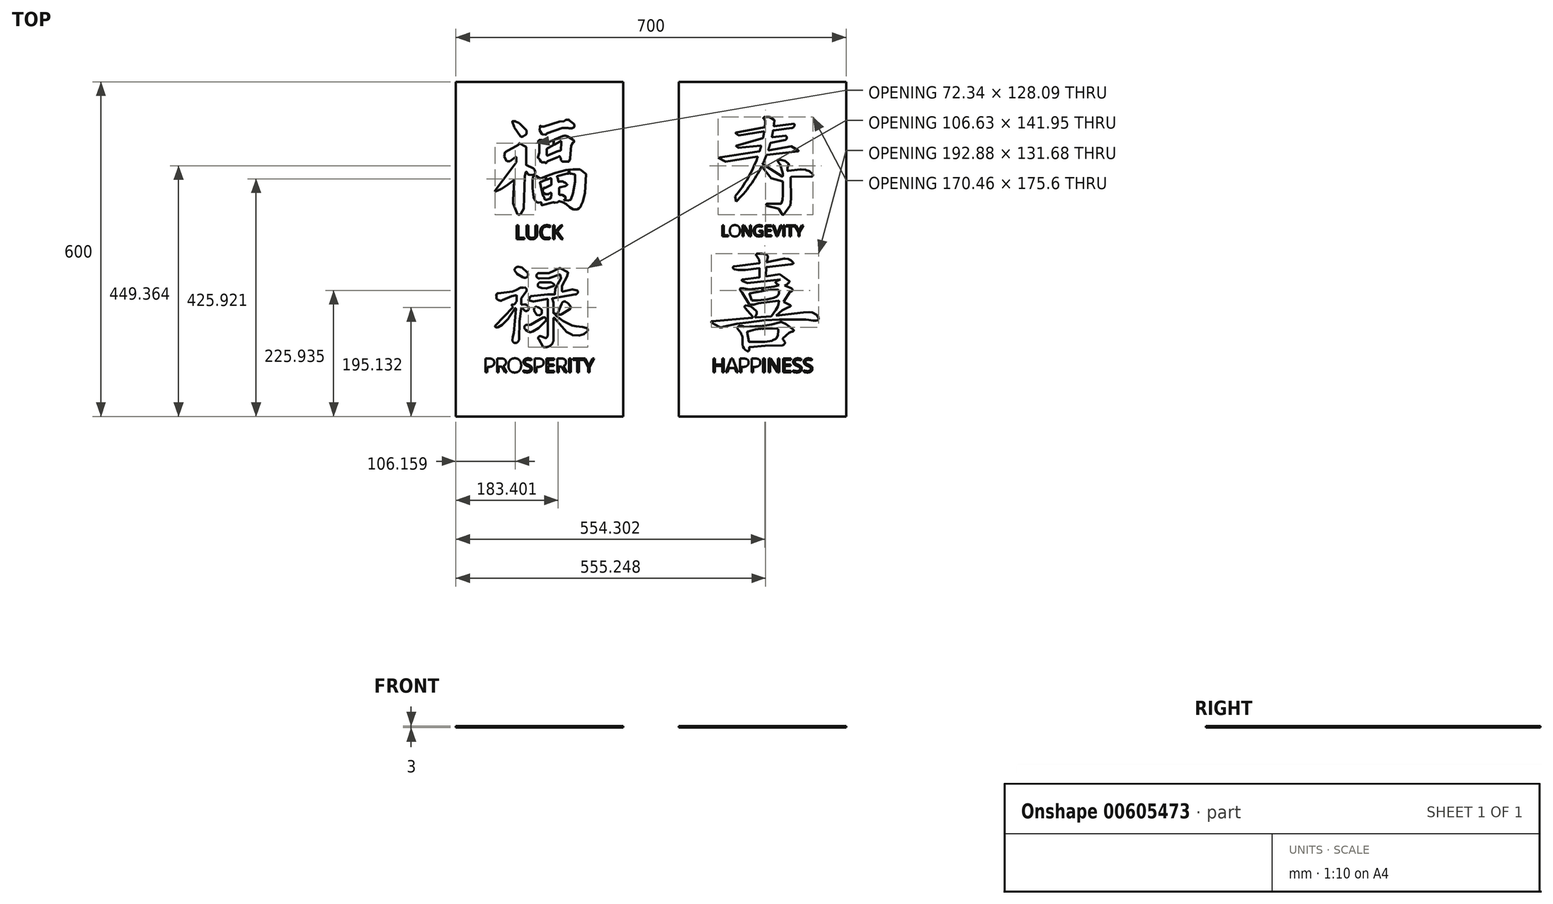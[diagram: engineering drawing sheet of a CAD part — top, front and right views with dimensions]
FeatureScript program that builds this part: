
annotation { "Feature Type Name" : "Feature", "Feature Type Description" : "" }
export const myFeature = defineFeature(function(context is Context, id is Id, definition is map)
    precondition{}
    {
        {
            var Q0;
            Q0=qCreatedBy(makeId("Top.planeOp"),FACE);
            var sketch = newSketch(context, id + "F0", { "sketchPlane" : qUnion([Q0])});
            skLineSegment(sketch, "E0.bottom", {"start": v(-350, 0) * mm, "end": v(-50, 0) * mm});
            skLineSegment(sketch, "E0.top", {"start": v(-350, -600) * mm, "end": v(-50, -600) * mm});
            skLineSegment(sketch, "E0.left", {"start": v(-350, 0) * mm, "end": v(-350, -600) * mm});
            skLineSegment(sketch, "E0.right", {"start": v(-50, 0) * mm, "end": v(-50, -600) * mm});
            skLineSegment(sketch, "E1.bottom", {"start": v(50, 0) * mm, "end": v(350, 0) * mm});
            skLineSegment(sketch, "E1.top", {"start": v(50, -600) * mm, "end": v(350, -600) * mm});
            skLineSegment(sketch, "E1.left", {"start": v(50, 0) * mm, "end": v(50, -600) * mm});
            skLineSegment(sketch, "E1.right", {"start": v(350, 0) * mm, "end": v(350, -600) * mm});
            skPoint(sketch, "E2", {"position": v(200, -322.19) * mm});
            skPoint(sketch, "E3", {"position": v(200, 889.4) * mm});
            skPoint(sketch, "E4", {"position": v(-200, -50.96) * mm});
            skPoint(sketch, "E5", {"position": v(-200, -322.19) * mm});
            skPoint(sketch, "E6", {"position": v(-200, 0) * mm});
            skPoint(sketch, "E7", {"position": v(200, 0) * mm});
            skArc(sketch, "E8", {"start": v(150.97, -205.38) * mm, "mid": v(173.95, -172.12) * mm, "end": v(191.01, -135.48) * mm});
            skLineSegment(sketch, "E9", {"start": v(203.27, -81.17) * mm, "end": v(152.4, -90.81) * mm});
            skLineSegment(sketch, "E10", {"start": v(152.1, -92.04) * mm, "end": v(157.18, -95.91) * mm});
            skLineSegment(sketch, "E11", {"start": v(157.7, -96.04) * mm, "end": v(201.62, -88.88) * mm});
            skLineSegment(sketch, "E12", {"start": v(200.2, -101.22) * mm, "end": v(153.27, -114.59) * mm});
            skLineSegment(sketch, "E13", {"start": v(153.04, -115.8) * mm, "end": v(155.79, -117.9) * mm});
            skLineSegment(sketch, "E14", {"start": v(156.27, -118.03) * mm, "end": v(196.3, -114.2) * mm});
            skLineSegment(sketch, "E15", {"start": v(194.19, -124.37) * mm, "end": v(120.02, -135.85) * mm});
            skLineSegment(sketch, "E16", {"start": v(120.02, -135.85) * mm, "end": v(133.53, -142.76) * mm});
            skLineSegment(sketch, "E17", {"start": v(133.94, -142.83) * mm, "end": v(189.92, -134.14) * mm});
            skArc(sketch, "E18", {"start": v(152.3, -214.99) * mm, "mid": v(178.07, -185.08) * mm, "end": v(198.4, -151.23) * mm});
            skPoint(sketch, "E19.visualSharp", {"position": v(150.97, -216.28) * mm});
            skPoint(sketch, "E20.visualSharp", {"position": v(133.72, -142.87) * mm});
            skArc(sketch, "E20.filletArc", {"start": v(133.53, -142.76) * mm, "mid": v(133.73, -142.83) * mm, "end": v(133.94, -142.83) * mm});
            skPoint(sketch, "E21.visualSharp", {"position": v(150.88, -91.1) * mm});
            skArc(sketch, "E21.filletArc", {"start": v(152.4, -90.81) * mm, "mid": v(151.85, -91.33) * mm, "end": v(152.1, -92.04) * mm});
            skPoint(sketch, "E22.visualSharp", {"position": v(157.41, -96.1) * mm});
            skArc(sketch, "E22.filletArc", {"start": v(157.18, -95.91) * mm, "mid": v(157.43, -96.03) * mm, "end": v(157.7, -96.04) * mm});
            skPoint(sketch, "E23.visualSharp", {"position": v(151.95, -114.96) * mm});
            skArc(sketch, "E23.filletArc", {"start": v(153.27, -114.59) * mm, "mid": v(152.78, -115.12) * mm, "end": v(153.04, -115.8) * mm});
            skPoint(sketch, "E24.visualSharp", {"position": v(156, -118.06) * mm});
            skArc(sketch, "E24.filletArc", {"start": v(155.79, -117.9) * mm, "mid": v(156.02, -118) * mm, "end": v(156.27, -118.03) * mm});
            skLineSegment(sketch, "E25", {"start": v(221.32, -79.5) * mm, "end": v(256.8, -75.2) * mm});
            skLineSegment(sketch, "E26", {"start": v(219.7, -86.87) * mm, "end": v(252.22, -82.93) * mm});
            skLineSegment(sketch, "E27", {"start": v(217.95, -99.22) * mm, "end": v(240.6, -96.47) * mm});
            skLineSegment(sketch, "E28", {"start": v(214.7, -109.29) * mm, "end": v(240.46, -104.07) * mm});
            skPoint(sketch, "E29.visualSharp", {"position": v(243.08, -103.54) * mm});
            skLineSegment(sketch, "E30", {"start": v(211.69, -122.58) * mm, "end": v(251.31, -115.55) * mm});
            skLineSegment(sketch, "E31", {"start": v(252, -115.67) * mm, "end": v(264.03, -122.7) * mm});
            skLineSegment(sketch, "E32", {"start": v(263.63, -124.55) * mm, "end": v(207.84, -130.7) * mm});
            skPoint(sketch, "E33.visualSharp", {"position": v(251.67, -115.49) * mm});
            skArc(sketch, "E33.filletArc", {"start": v(252, -115.67) * mm, "mid": v(251.66, -115.55) * mm, "end": v(251.31, -115.55) * mm});
            skPoint(sketch, "E34.visualSharp", {"position": v(266.64, -124.22) * mm});
            skArc(sketch, "E34.filletArc", {"start": v(263.63, -124.55) * mm, "mid": v(264.5, -123.76) * mm, "end": v(264.03, -122.7) * mm});
            skLineSegment(sketch, "E35", {"start": v(220.56, -75.45) * mm, "end": v(221.27, -69.14) * mm});
            skLineSegment(sketch, "E36", {"start": v(220.8, -68.17) * mm, "end": v(212.05, -62.97) * mm});
            skLineSegment(sketch, "E37", {"start": v(211.54, -62.83) * mm, "end": v(204.36, -62.83) * mm});
            skLineSegment(sketch, "E38", {"start": v(204.65, -74.72) * mm, "end": v(204.65, -69.48) * mm});
            skLineSegment(sketch, "E39", {"start": v(204.34, -68.75) * mm, "end": v(201.84, -66.36) * mm});
            skArc(sketch, "E40", {"start": v(204.36, -62.83) * mm, "mid": v(202.37, -63.65) * mm, "end": v(201.53, -65.62) * mm});
            skPoint(sketch, "E41.visualSharp", {"position": v(201.56, -66.1) * mm});
            skArc(sketch, "E41.filletArc", {"start": v(201.53, -65.62) * mm, "mid": v(201.6, -66.02) * mm, "end": v(201.84, -66.36) * mm});
            skPoint(sketch, "E42.visualSharp", {"position": v(211.82, -62.83) * mm});
            skArc(sketch, "E42.filletArc", {"start": v(212.05, -62.97) * mm, "mid": v(211.8, -62.87) * mm, "end": v(211.54, -62.83) * mm});
            skPoint(sketch, "E43.visualSharp", {"position": v(221.35, -68.5) * mm});
            skArc(sketch, "E43.filletArc", {"start": v(221.27, -69.14) * mm, "mid": v(221.18, -68.58) * mm, "end": v(220.8, -68.17) * mm});
            skPoint(sketch, "E44.visualSharp", {"position": v(204.65, -69.05) * mm});
            skArc(sketch, "E44.filletArc", {"start": v(204.65, -69.48) * mm, "mid": v(204.57, -69.08) * mm, "end": v(204.34, -68.75) * mm});
            skArc(sketch, "E45.trimOffspring", {"start": v(220.2, -78.38) * mm, "mid": v(220.38, -76.92) * mm, "end": v(220.56, -75.45) * mm});
            skArc(sketch, "E46.trimOffspring", {"start": v(204.08, -80.3) * mm, "mid": v(204.38, -77.5) * mm, "end": v(204.65, -74.72) * mm});
            skArc(sketch, "E47.trimOffspring", {"start": v(216.85, -98.01) * mm, "mid": v(217.9, -92.87) * mm, "end": v(218.83, -87.7) * mm});
            skArc(sketch, "E48.trimOffspring", {"start": v(200.9, -100.46) * mm, "mid": v(201.9, -95.25) * mm, "end": v(202.77, -90.02) * mm});
            skArc(sketch, "E49.trimOffspring", {"start": v(210.56, -121.28) * mm, "mid": v(212.32, -115.66) * mm, "end": v(213.94, -110) * mm});
            skArc(sketch, "E50.trimOffspring", {"start": v(195, -123.67) * mm, "mid": v(196.22, -119.58) * mm, "end": v(197.37, -115.46) * mm});
            skPoint(sketch, "E51.visualSharp", {"position": v(204, -81.03) * mm});
            skArc(sketch, "E51.filletArc", {"start": v(203.27, -81.17) * mm, "mid": v(203.82, -80.87) * mm, "end": v(204.08, -80.3) * mm});
            skPoint(sketch, "E52.visualSharp", {"position": v(220.04, -79.65) * mm});
            skArc(sketch, "E52.filletArc", {"start": v(220.2, -78.38) * mm, "mid": v(220.49, -79.21) * mm, "end": v(221.32, -79.5) * mm});
            skPoint(sketch, "E53.visualSharp", {"position": v(218.95, -86.96) * mm});
            skArc(sketch, "E53.filletArc", {"start": v(219.7, -86.87) * mm, "mid": v(219.12, -87.14) * mm, "end": v(218.83, -87.7) * mm});
            skArc(sketch, "E54.filletArc", {"start": v(202.77, -90.02) * mm, "mid": v(202.48, -89.15) * mm, "end": v(201.62, -88.88) * mm});
            skPoint(sketch, "E55.visualSharp", {"position": v(214.1, -109.4) * mm});
            skArc(sketch, "E55.filletArc", {"start": v(214.7, -109.29) * mm, "mid": v(214.22, -109.54) * mm, "end": v(213.94, -110) * mm});
            skPoint(sketch, "E56.visualSharp", {"position": v(216.55, -99.39) * mm});
            skArc(sketch, "E56.filletArc", {"start": v(216.85, -98.01) * mm, "mid": v(217.1, -98.9) * mm, "end": v(217.95, -99.22) * mm});
            skPoint(sketch, "E57.visualSharp", {"position": v(200.78, -101.06) * mm});
            skArc(sketch, "E57.filletArc", {"start": v(200.2, -101.22) * mm, "mid": v(200.65, -100.94) * mm, "end": v(200.9, -100.46) * mm});
            skPoint(sketch, "E58.visualSharp", {"position": v(197.74, -114.07) * mm});
            skArc(sketch, "E58.filletArc", {"start": v(197.37, -115.46) * mm, "mid": v(197.16, -114.56) * mm, "end": v(196.3, -114.2) * mm});
            skPoint(sketch, "E59.visualSharp", {"position": v(210.04, -122.87) * mm});
            skArc(sketch, "E59.filletArc", {"start": v(210.56, -121.28) * mm, "mid": v(210.76, -122.25) * mm, "end": v(211.69, -122.58) * mm});
            skPoint(sketch, "E60.visualSharp", {"position": v(194.8, -124.27) * mm});
            skArc(sketch, "E60.filletArc", {"start": v(194.19, -124.37) * mm, "mid": v(194.69, -124.14) * mm, "end": v(195, -123.67) * mm});
            skPoint(sketch, "E61.visualSharp", {"position": v(207.23, -130.77) * mm});
            skArc(sketch, "E61.filletArc", {"start": v(207.84, -130.7) * mm, "mid": v(207.34, -130.91) * mm, "end": v(207.01, -131.35) * mm});
            skPoint(sketch, "E62.visualSharp", {"position": v(191.59, -133.88) * mm});
            skArc(sketch, "E62.filletArc", {"start": v(191.01, -135.48) * mm, "mid": v(190.85, -134.5) * mm, "end": v(189.92, -134.14) * mm});
            skLineSegment(sketch, "E63", {"start": v(236.4, -202.56) * mm, "end": v(236.4, -178.81) * mm});
            skLineSegment(sketch, "E64", {"start": v(236.35, -164.48) * mm, "end": v(231.15, -147.17) * mm});
            skLineSegment(sketch, "E65", {"start": v(230.92, -146.78) * mm, "end": v(226.96, -142.52) * mm});
            skLineSegment(sketch, "E66", {"start": v(228.2, -139.57) * mm, "end": v(232.25, -139.57) * mm});
            skLineSegment(sketch, "E67", {"start": v(232.54, -139.61) * mm, "end": v(240, -141.85) * mm});
            skLineSegment(sketch, "E68", {"start": v(240.3, -142) * mm, "end": v(246.08, -146.34) * mm});
            skLineSegment(sketch, "E69", {"start": v(246.46, -146.92) * mm, "end": v(246.91, -148.97) * mm});
            skLineSegment(sketch, "E70", {"start": v(246.8, -149.7) * mm, "end": v(244.96, -152.72) * mm});
            skLineSegment(sketch, "E71", {"start": v(244.82, -153.24) * mm, "end": v(244.82, -158.86) * mm});
            skLineSegment(sketch, "E72", {"start": v(245.95, -159.86) * mm, "end": v(268.33, -156.78) * mm});
            skLineSegment(sketch, "E73", {"start": v(268.6, -156.78) * mm, "end": v(277.5, -157.95) * mm});
            skLineSegment(sketch, "E74", {"start": v(277.7, -158) * mm, "end": v(283.92, -160.22) * mm});
            skLineSegment(sketch, "E75", {"start": v(284.29, -160.44) * mm, "end": v(290.1, -166.12) * mm});
            skLineSegment(sketch, "E76", {"start": v(287.91, -169.95) * mm, "end": v(251.6, -170.63) * mm});
            skLineSegment(sketch, "E77", {"start": v(250.6, -171.65) * mm, "end": v(251.33, -209.98) * mm});
            skLineSegment(sketch, "E78", {"start": v(251.33, -209.98) * mm, "end": v(251.22, -210.71) * mm});
            skLineSegment(sketch, "E79", {"start": v(251.22, -210.71) * mm, "end": v(249.58, -222.08) * mm});
            skLineSegment(sketch, "E80", {"start": v(249.38, -222.55) * mm, "end": v(237.4, -238.05) * mm});
            skLineSegment(sketch, "E81", {"start": v(235.76, -237.98) * mm, "end": v(228.89, -227.27) * mm});
            skLineSegment(sketch, "E82", {"start": v(228.89, -227.27) * mm, "end": v(208, -222.39) * mm});
            skLineSegment(sketch, "E83", {"start": v(208.92, -218.5) * mm, "end": v(233.02, -218.32) * mm});
            skLineSegment(sketch, "E84", {"start": v(233.98, -217.57) * mm, "end": v(235.56, -211.62) * mm});
            skLineSegment(sketch, "E85", {"start": v(235.6, -211.45) * mm, "end": v(236.4, -202.65) * mm});
            skArc(sketch, "E86", {"start": v(208.92, -218.5) * mm, "mid": v(206.52, -220) * mm, "end": v(208, -222.39) * mm});
            skLineSegment(sketch, "E87", {"start": v(234.87, -169.4) * mm, "end": v(200.05, -147.79) * mm});
            skLineSegment(sketch, "E88", {"start": v(198.4, -151.23) * mm, "end": v(215.23, -173.01) * mm});
            skPoint(sketch, "E89.visualSharp", {"position": v(210.3, -166.64) * mm});
            skPoint(sketch, "E90.visualSharp", {"position": v(232.83, -176.15) * mm});
            skPoint(sketch, "E91.visualSharp", {"position": v(231.08, -146.95) * mm});
            skArc(sketch, "E91.filletArc", {"start": v(231.15, -147.17) * mm, "mid": v(231.06, -146.96) * mm, "end": v(230.92, -146.78) * mm});
            skPoint(sketch, "E92.visualSharp", {"position": v(236.4, -164.62) * mm});
            skArc(sketch, "E92.filletArc", {"start": v(236.4, -164.77) * mm, "mid": v(236.39, -164.62) * mm, "end": v(236.35, -164.48) * mm});
            skPoint(sketch, "E93.visualSharp", {"position": v(244.82, -152.96) * mm});
            skArc(sketch, "E93.filletArc", {"start": v(244.96, -152.72) * mm, "mid": v(244.85, -152.97) * mm, "end": v(244.82, -153.24) * mm});
            skPoint(sketch, "E94.visualSharp", {"position": v(247, -149.36) * mm});
            skArc(sketch, "E94.filletArc", {"start": v(246.8, -149.7) * mm, "mid": v(246.92, -149.35) * mm, "end": v(246.91, -148.97) * mm});
            skPoint(sketch, "E95.visualSharp", {"position": v(246.38, -146.56) * mm});
            skArc(sketch, "E95.filletArc", {"start": v(246.46, -146.92) * mm, "mid": v(246.32, -146.6) * mm, "end": v(246.08, -146.34) * mm});
            skPoint(sketch, "E96.visualSharp", {"position": v(240.17, -141.9) * mm});
            skArc(sketch, "E96.filletArc", {"start": v(240.3, -142) * mm, "mid": v(240.16, -141.92) * mm, "end": v(240, -141.85) * mm});
            skPoint(sketch, "E97.visualSharp", {"position": v(232.4, -139.57) * mm});
            skArc(sketch, "E97.filletArc", {"start": v(232.54, -139.61) * mm, "mid": v(232.4, -139.58) * mm, "end": v(232.25, -139.57) * mm});
            skArc(sketch, "E98", {"start": v(228.2, -139.57) * mm, "mid": v(226.63, -140.65) * mm, "end": v(226.96, -142.52) * mm});
            skLineSegment(sketch, "E99.trimOffspring", {"start": v(236.4, -168.56) * mm, "end": v(236.4, -164.77) * mm});
            skPoint(sketch, "E100.visualSharp", {"position": v(236.4, -170.36) * mm});
            skArc(sketch, "E100.filletArc", {"start": v(234.87, -169.4) * mm, "mid": v(235.88, -169.43) * mm, "end": v(236.4, -168.56) * mm});
            skPoint(sketch, "E101.visualSharp", {"position": v(244.82, -160.01) * mm});
            skArc(sketch, "E101.filletArc", {"start": v(244.82, -158.86) * mm, "mid": v(245.16, -159.62) * mm, "end": v(245.95, -159.86) * mm});
            skPoint(sketch, "E102.visualSharp", {"position": v(250.6, -170.65) * mm});
            skArc(sketch, "E102.filletArc", {"start": v(251.6, -170.63) * mm, "mid": v(250.89, -170.93) * mm, "end": v(250.6, -171.65) * mm});
            skPoint(sketch, "E103.visualSharp", {"position": v(236.4, -190.47) * mm});
            skPoint(sketch, "E104.visualSharp", {"position": v(268.46, -156.76) * mm});
            skArc(sketch, "E104.filletArc", {"start": v(268.6, -156.78) * mm, "mid": v(268.46, -156.77) * mm, "end": v(268.33, -156.78) * mm});
            skPoint(sketch, "E105.visualSharp", {"position": v(277.6, -157.96) * mm});
            skArc(sketch, "E105.filletArc", {"start": v(277.7, -158) * mm, "mid": v(277.6, -157.97) * mm, "end": v(277.5, -157.95) * mm});
            skPoint(sketch, "E106.visualSharp", {"position": v(284.13, -160.3) * mm});
            skArc(sketch, "E106.filletArc", {"start": v(284.29, -160.44) * mm, "mid": v(284.12, -160.31) * mm, "end": v(283.92, -160.22) * mm});
            skArc(sketch, "E107", {"start": v(287.91, -169.95) * mm, "mid": v(290, -168.85) * mm, "end": v(290.36, -166.53) * mm});
            skPoint(sketch, "E108.visualSharp", {"position": v(290.27, -166.27) * mm});
            skArc(sketch, "E108.filletArc", {"start": v(290.36, -166.53) * mm, "mid": v(290.26, -166.3) * mm, "end": v(290.1, -166.12) * mm});
            skPoint(sketch, "E109.visualSharp", {"position": v(235.58, -211.54) * mm});
            skArc(sketch, "E109.filletArc", {"start": v(235.56, -211.62) * mm, "mid": v(235.58, -211.54) * mm, "end": v(235.6, -211.45) * mm});
            skPoint(sketch, "E110.visualSharp", {"position": v(236.4, -202.6) * mm});
            skArc(sketch, "E110.filletArc", {"start": v(236.4, -202.65) * mm, "mid": v(236.4, -202.6) * mm, "end": v(236.4, -202.56) * mm});
            skPoint(sketch, "E111.visualSharp", {"position": v(233.78, -218.31) * mm});
            skArc(sketch, "E111.filletArc", {"start": v(233.02, -218.32) * mm, "mid": v(233.62, -218.1) * mm, "end": v(233.98, -217.57) * mm});
            skPoint(sketch, "E112.visualSharp", {"position": v(249.54, -222.34) * mm});
            skArc(sketch, "E112.filletArc", {"start": v(249.38, -222.55) * mm, "mid": v(249.51, -222.33) * mm, "end": v(249.58, -222.08) * mm});
            skPoint(sketch, "E113.visualSharp", {"position": v(250.6, -215.07) * mm});
            skLineSegment(sketch, "E113.filletArc", {"start": v(251.22, -210.71) * mm, "end": v(251.22, -210.71) * mm});
            skPoint(sketch, "E114.visualSharp", {"position": v(234.79, -236.46) * mm});
            skLineSegment(sketch, "E115", {"start": v(206.79, -324.76) * mm, "end": v(206.79, -322.64) * mm});
            skLineSegment(sketch, "E116", {"start": v(206.79, -324.76) * mm, "end": v(209.26, -315.5) * mm});
            skLineSegment(sketch, "E117", {"start": v(205.94, -309.66) * mm, "end": v(199.02, -308.22) * mm});
            skLineSegment(sketch, "E118", {"start": v(199.02, -308.22) * mm, "end": v(190.8, -308.22) * mm});
            skLineSegment(sketch, "E119", {"start": v(193.97, -318.77) * mm, "end": v(188.57, -311.62) * mm});
            skLineSegment(sketch, "E120", {"start": v(194.17, -319.3) * mm, "end": v(194.58, -324.5) * mm});
            skLineSegment(sketch, "E121", {"start": v(193.7, -325.58) * mm, "end": v(149.02, -330.78) * mm});
            skLineSegment(sketch, "E122", {"start": v(147.17, -334.1) * mm, "end": v(149.2, -336.14) * mm});
            skLineSegment(sketch, "E123", {"start": v(149.2, -336.14) * mm, "end": v(156.22, -337.61) * mm});
            skLineSegment(sketch, "E124", {"start": v(156.22, -337.61) * mm, "end": v(168.97, -337.61) * mm});
            skLineSegment(sketch, "E125", {"start": v(168.97, -337.61) * mm, "end": v(193.7, -334.35) * mm});
            skLineSegment(sketch, "E126", {"start": v(194.83, -335.34) * mm, "end": v(194.83, -349.81) * mm});
            skLineSegment(sketch, "E127", {"start": v(193.95, -350.8) * mm, "end": v(164.25, -354.23) * mm});
            skLineSegment(sketch, "E128", {"start": v(163.67, -357.23) * mm, "end": v(172.73, -360.64) * mm});
            skLineSegment(sketch, "E129", {"start": v(172.73, -360.64) * mm, "end": v(232.3, -354.46) * mm});
            skLineSegment(sketch, "E130", {"start": v(222.37, -357.99) * mm, "end": v(232.3, -354.46) * mm});
            skLineSegment(sketch, "E131", {"start": v(248.66, -357.47) * mm, "end": v(230.64, -345.03) * mm});
            skLineSegment(sketch, "E132", {"start": v(230.64, -345.03) * mm, "end": v(206.9, -348.46) * mm});
            skLineSegment(sketch, "E133", {"start": v(205.75, -347.43) * mm, "end": v(206.4, -332.96) * mm});
            skLineSegment(sketch, "E134", {"start": v(207.3, -332.01) * mm, "end": v(250.74, -327.37) * mm});
            skLineSegment(sketch, "E135", {"start": v(250.74, -327.37) * mm, "end": v(253.77, -326.67) * mm});
            skLineSegment(sketch, "E136", {"start": v(254.7, -323.72) * mm, "end": v(250.9, -320.07) * mm});
            skLineSegment(sketch, "E137", {"start": v(250.9, -320.07) * mm, "end": v(246.21, -317.94) * mm});
            skLineSegment(sketch, "E138", {"start": v(246.21, -317.94) * mm, "end": v(240.47, -317.15) * mm});
            skLineSegment(sketch, "E139", {"start": v(240.47, -317.15) * mm, "end": v(238.33, -317.15) * mm});
            skLineSegment(sketch, "E140", {"start": v(238.33, -317.15) * mm, "end": v(208, -323.62) * mm});
            skArc(sketch, "E141", {"start": v(222.37, -357.99) * mm, "mid": v(235.67, -365.74) * mm, "end": v(248.66, -357.47) * mm});
            skArc(sketch, "E142", {"start": v(253.77, -326.67) * mm, "mid": v(255.16, -325.49) * mm, "end": v(254.7, -323.72) * mm});
            skArc(sketch, "E143", {"start": v(209.26, -315.5) * mm, "mid": v(208.92, -311.83) * mm, "end": v(205.94, -309.66) * mm});
            skArc(sketch, "E144", {"start": v(190.8, -308.22) * mm, "mid": v(188.76, -309.32) * mm, "end": v(188.57, -311.62) * mm});
            skArc(sketch, "E145", {"start": v(149.02, -330.78) * mm, "mid": v(147.24, -331.97) * mm, "end": v(147.17, -334.1) * mm});
            skArc(sketch, "E146", {"start": v(164.25, -354.23) * mm, "mid": v(162.86, -355.52) * mm, "end": v(163.67, -357.23) * mm});
            skLineSegment(sketch, "E147", {"start": v(175.47, -372.3) * mm, "end": v(198.63, -369.76) * mm});
            skLineSegment(sketch, "E148", {"start": v(220.66, -367.34) * mm, "end": v(230.72, -363.81) * mm});
            skLineSegment(sketch, "E149", {"start": v(230.72, -363.81) * mm, "end": v(234.51, -363.81) * mm});
            skLineSegment(sketch, "E150", {"start": v(234.51, -363.81) * mm, "end": v(239.01, -364.72) * mm});
            skLineSegment(sketch, "E151", {"start": v(239.01, -364.72) * mm, "end": v(252.04, -370.48) * mm});
            skLineSegment(sketch, "E152", {"start": v(249.71, -375.74) * mm, "end": v(237.97, -394.34) * mm});
            skLineSegment(sketch, "E153", {"start": v(237.97, -394.34) * mm, "end": v(250.14, -401.01) * mm});
            skLineSegment(sketch, "E154", {"start": v(243.94, -405.05) * mm, "end": v(235.45, -409.87) * mm});
            skLineSegment(sketch, "E155", {"start": v(235.45, -409.87) * mm, "end": v(229.9, -413.94) * mm});
            skLineSegment(sketch, "E156", {"start": v(229.9, -413.94) * mm, "end": v(224.27, -419.57) * mm});
            skLineSegment(sketch, "E157", {"start": v(224.27, -419.57) * mm, "end": v(273.02, -413.63) * mm});
            skLineSegment(sketch, "E158", {"start": v(273.02, -413.63) * mm, "end": v(283.46, -412.76) * mm});
            skLineSegment(sketch, "E159", {"start": v(283.46, -412.76) * mm, "end": v(289.2, -413.54) * mm});
            skLineSegment(sketch, "E160", {"start": v(289.2, -413.54) * mm, "end": v(297.19, -417.92) * mm});
            skLineSegment(sketch, "E161", {"start": v(297.19, -417.92) * mm, "end": v(300.74, -422.77) * mm});
            skLineSegment(sketch, "E162", {"start": v(300.74, -422.77) * mm, "end": v(300.74, -425.73) * mm});
            skLineSegment(sketch, "E163", {"start": v(300.74, -425.73) * mm, "end": v(298.89, -427.59) * mm});
            skLineSegment(sketch, "E164", {"start": v(298.89, -427.59) * mm, "end": v(296.18, -428.14) * mm});
            skLineSegment(sketch, "E165", {"start": v(296.18, -428.14) * mm, "end": v(290.12, -428.14) * mm});
            skLineSegment(sketch, "E166", {"start": v(290.12, -428.14) * mm, "end": v(282.51, -426.82) * mm});
            skLineSegment(sketch, "E167", {"start": v(282.51, -426.82) * mm, "end": v(277.46, -425.97) * mm});
            skLineSegment(sketch, "E168", {"start": v(277.46, -425.97) * mm, "end": v(229.98, -425.97) * mm});
            skLineSegment(sketch, "E169", {"start": v(229.98, -425.97) * mm, "end": v(203.95, -427.55) * mm});
            skLineSegment(sketch, "E170", {"start": v(203.95, -427.55) * mm, "end": v(174.55, -431.17) * mm});
            skLineSegment(sketch, "E171", {"start": v(174.55, -431.17) * mm, "end": v(154.02, -434.06) * mm});
            skLineSegment(sketch, "E172", {"start": v(154.02, -434.06) * mm, "end": v(130.64, -439.15) * mm});
            skLineSegment(sketch, "E173", {"start": v(130.64, -439.15) * mm, "end": v(128.3, -439.86) * mm});
            skLineSegment(sketch, "E174", {"start": v(128.01, -439.9) * mm, "end": v(123.07, -439.9) * mm});
            skLineSegment(sketch, "E175", {"start": v(122.6, -439.78) * mm, "end": v(108.69, -432.16) * mm});
            skLineSegment(sketch, "E176", {"start": v(109.24, -429.14) * mm, "end": v(181.48, -423.06) * mm});
            skLineSegment(sketch, "E177", {"start": v(182.16, -421.42) * mm, "end": v(168.34, -404.98) * mm});
            skPoint(sketch, "E178", {"position": v(168.01, -402.4) * mm});
            skLineSegment(sketch, "E179", {"start": v(169.41, -401.14) * mm, "end": v(174.11, -401.53) * mm});
            skLineSegment(sketch, "E180", {"start": v(174.11, -401.53) * mm, "end": v(177.2, -402.04) * mm});
            skLineSegment(sketch, "E181", {"start": v(177.2, -402.04) * mm, "end": v(179.42, -403) * mm});
            skLineSegment(sketch, "E182", {"start": v(179.42, -403) * mm, "end": v(188.9, -411.09) * mm});
            skLineSegment(sketch, "E183", {"start": v(188.9, -411.09) * mm, "end": v(189.44, -412.41) * mm});
            skLineSegment(sketch, "E184", {"start": v(189.44, -412.41) * mm, "end": v(189.44, -416.06) * mm});
            skLineSegment(sketch, "E185", {"start": v(189.44, -416.06) * mm, "end": v(187.22, -421.36) * mm});
            skLineSegment(sketch, "E186", {"start": v(188.23, -422.74) * mm, "end": v(215.19, -420.24) * mm});
            skLineSegment(sketch, "E187", {"start": v(215.9, -419.84) * mm, "end": v(223.65, -409.38) * mm});
            skLineSegment(sketch, "E188", {"start": v(223.65, -409.38) * mm, "end": v(227.7, -402.55) * mm});
            skLineSegment(sketch, "E189", {"start": v(227.7, -402.55) * mm, "end": v(228.97, -397.84) * mm});
            skLineSegment(sketch, "E190", {"start": v(228.97, -397.84) * mm, "end": v(229.38, -393.54) * mm});
            skLineSegment(sketch, "E191", {"start": v(228.25, -392.45) * mm, "end": v(192.82, -397.1) * mm});
            skLineSegment(sketch, "E192", {"start": v(192.82, -397.1) * mm, "end": v(184.51, -399.27) * mm});
            skLineSegment(sketch, "E193", {"start": v(184.51, -399.27) * mm, "end": v(182.17, -399.5) * mm});
            skLineSegment(sketch, "E194", {"start": v(182.17, -399.5) * mm, "end": v(177.24, -399.5) * mm});
            skLineSegment(sketch, "E195", {"start": v(177.24, -399.5) * mm, "end": v(176.3, -399.08) * mm});
            skLineSegment(sketch, "E196", {"start": v(176.3, -399.08) * mm, "end": v(163.42, -378.13) * mm});
            skLineSegment(sketch, "E197", {"start": v(163.42, -378.13) * mm, "end": v(159.8, -373.41) * mm});
            skLineSegment(sketch, "E198", {"start": v(161.21, -370.13) * mm, "end": v(166.22, -370.13) * mm});
            skLineSegment(sketch, "E199", {"start": v(166.22, -370.13) * mm, "end": v(175.47, -372.3) * mm});
            skArc(sketch, "E200", {"start": v(161.21, -370.13) * mm, "mid": v(159.53, -371.35) * mm, "end": v(159.8, -373.41) * mm});
            skArc(sketch, "E201", {"start": v(249.71, -375.74) * mm, "mid": v(253.5, -374.27) * mm, "end": v(252.04, -370.48) * mm});
            skArc(sketch, "E202", {"start": v(168.01, -402.4) * mm, "mid": v(167.98, -403.71) * mm, "end": v(168.34, -404.98) * mm});
            skArc(sketch, "E203", {"start": v(168.76, -401.32) * mm, "mid": v(168.29, -401.79) * mm, "end": v(168.01, -402.4) * mm});
            skArc(sketch, "E204", {"start": v(109.24, -429.14) * mm, "mid": v(107.87, -430.45) * mm, "end": v(108.69, -432.16) * mm});
            skLineSegment(sketch, "E205", {"start": v(177.42, -379.2) * mm, "end": v(198.9, -375.5) * mm});
            skLineSegment(sketch, "E206", {"start": v(213.91, -372.92) * mm, "end": v(227.23, -372.92) * mm});
            skLineSegment(sketch, "E207", {"start": v(176.65, -380.51) * mm, "end": v(180.66, -392.03) * mm});
            skLineSegment(sketch, "E208", {"start": v(180.66, -392.03) * mm, "end": v(191.53, -392.03) * mm});
            skLineSegment(sketch, "E209", {"start": v(191.53, -392.03) * mm, "end": v(208.45, -389.83) * mm});
            skLineSegment(sketch, "E210", {"start": v(208.45, -389.83) * mm, "end": v(219.87, -387.3) * mm});
            skLineSegment(sketch, "E211", {"start": v(219.87, -387.3) * mm, "end": v(225.47, -385.22) * mm});
            skLineSegment(sketch, "E212", {"start": v(228.55, -381.04) * mm, "end": v(229.43, -378.63) * mm});
            skLineSegment(sketch, "E213", {"start": v(229.43, -378.63) * mm, "end": v(229.2, -374.78) * mm});
            skArc(sketch, "E214", {"start": v(225.47, -385.22) * mm, "mid": v(227.31, -383.35) * mm, "end": v(228.55, -381.04) * mm});
            skArc(sketch, "E215", {"start": v(229.2, -374.78) * mm, "mid": v(228.59, -373.46) * mm, "end": v(227.23, -372.92) * mm});
            skPoint(sketch, "E216.visualSharp", {"position": v(194.15, -319) * mm});
            skArc(sketch, "E216.filletArc", {"start": v(194.17, -319.3) * mm, "mid": v(194.11, -319.02) * mm, "end": v(193.97, -318.77) * mm});
            skPoint(sketch, "E217.visualSharp", {"position": v(206.79, -323.87) * mm});
            skArc(sketch, "E217.filletArc", {"start": v(206.79, -322.64) * mm, "mid": v(207.16, -323.42) * mm, "end": v(208, -323.62) * mm});
            skPoint(sketch, "E218.visualSharp", {"position": v(194.66, -325.47) * mm});
            skArc(sketch, "E218.filletArc", {"start": v(193.7, -325.58) * mm, "mid": v(194.36, -325.22) * mm, "end": v(194.58, -324.5) * mm});
            skPoint(sketch, "E219.visualSharp", {"position": v(206.44, -332.1) * mm});
            skArc(sketch, "E219.filletArc", {"start": v(207.3, -332.01) * mm, "mid": v(206.67, -332.32) * mm, "end": v(206.4, -332.96) * mm});
            skPoint(sketch, "E220.visualSharp", {"position": v(194.83, -334.2) * mm});
            skArc(sketch, "E220.filletArc", {"start": v(194.83, -335.34) * mm, "mid": v(194.49, -334.59) * mm, "end": v(193.7, -334.35) * mm});
            skPoint(sketch, "E221.visualSharp", {"position": v(205.7, -348.64) * mm});
            skArc(sketch, "E221.filletArc", {"start": v(205.75, -347.43) * mm, "mid": v(206.08, -348.22) * mm, "end": v(206.9, -348.46) * mm});
            skPoint(sketch, "E222.visualSharp", {"position": v(194.83, -350.7) * mm});
            skArc(sketch, "E222.filletArc", {"start": v(193.95, -350.8) * mm, "mid": v(194.58, -350.48) * mm, "end": v(194.83, -349.81) * mm});
            skPoint(sketch, "E223.visualSharp", {"position": v(176.26, -379.4) * mm});
            skArc(sketch, "E223.filletArc", {"start": v(177.42, -379.2) * mm, "mid": v(176.73, -379.67) * mm, "end": v(176.65, -380.51) * mm});
            skPoint(sketch, "E224.visualSharp", {"position": v(213.83, -372.92) * mm});
            skArc(sketch, "E224.filletArc", {"start": v(213.91, -372.92) * mm, "mid": v(213.83, -372.92) * mm, "end": v(213.74, -372.93) * mm});
            skPoint(sketch, "E225.visualSharp", {"position": v(229.5, -392.29) * mm});
            skArc(sketch, "E225.filletArc", {"start": v(229.38, -393.54) * mm, "mid": v(229.08, -392.72) * mm, "end": v(228.25, -392.45) * mm});
            skPoint(sketch, "E226.visualSharp", {"position": v(215.63, -420.2) * mm});
            skArc(sketch, "E226.filletArc", {"start": v(215.19, -420.24) * mm, "mid": v(215.58, -420.12) * mm, "end": v(215.9, -419.84) * mm});
            skPoint(sketch, "E227.visualSharp", {"position": v(186.58, -422.9) * mm});
            skArc(sketch, "E227.filletArc", {"start": v(187.22, -421.36) * mm, "mid": v(187.34, -422.34) * mm, "end": v(188.23, -422.74) * mm});
            skPoint(sketch, "E228.visualSharp", {"position": v(183.4, -422.9) * mm});
            skArc(sketch, "E228.filletArc", {"start": v(181.48, -423.06) * mm, "mid": v(182.32, -422.44) * mm, "end": v(182.16, -421.42) * mm});
            skPoint(sketch, "E229.visualSharp", {"position": v(169.12, -401.11) * mm});
            skArc(sketch, "E229.filletArc", {"start": v(169.41, -401.14) * mm, "mid": v(169.07, -401.17) * mm, "end": v(168.76, -401.32) * mm});
            skPoint(sketch, "E230.visualSharp", {"position": v(122.82, -439.9) * mm});
            skArc(sketch, "E230.filletArc", {"start": v(122.6, -439.78) * mm, "mid": v(122.83, -439.87) * mm, "end": v(123.07, -439.9) * mm});
            skPoint(sketch, "E231.visualSharp", {"position": v(128.16, -439.9) * mm});
            skArc(sketch, "E231.filletArc", {"start": v(128.01, -439.9) * mm, "mid": v(128.16, -439.9) * mm, "end": v(128.3, -439.86) * mm});
            skLineSegment(sketch, "E232", {"start": v(176.2, -466.25) * mm, "end": v(203.6, -466.25) * mm});
            skLineSegment(sketch, "E233", {"start": v(203.76, -466.23) * mm, "end": v(217.36, -464.05) * mm});
            skLineSegment(sketch, "E234", {"start": v(217.68, -463.94) * mm, "end": v(224.33, -460.25) * mm});
            skLineSegment(sketch, "E235", {"start": v(224.72, -459.86) * mm, "end": v(227.22, -455.33) * mm});
            skLineSegment(sketch, "E236", {"start": v(227.35, -454.93) * mm, "end": v(228.11, -445.87) * mm});
            skLineSegment(sketch, "E237", {"start": v(225.37, -442.21) * mm, "end": v(201.33, -442.6) * mm});
            skLineSegment(sketch, "E238", {"start": v(201.33, -442.6) * mm, "end": v(199.98, -442.73) * mm});
            skLineSegment(sketch, "E239", {"start": v(186.83, -443.91) * mm, "end": v(173.33, -447.6) * mm});
            skLineSegment(sketch, "E240", {"start": v(172.6, -448.71) * mm, "end": v(175.2, -465.4) * mm});
            skArc(sketch, "E241", {"start": v(228.11, -445.87) * mm, "mid": v(227.44, -443.52) * mm, "end": v(225.37, -442.21) * mm});
            skPoint(sketch, "E242.visualSharp", {"position": v(172.47, -447.83) * mm});
            skArc(sketch, "E242.filletArc", {"start": v(173.33, -447.6) * mm, "mid": v(172.75, -448.02) * mm, "end": v(172.6, -448.71) * mm});
            skPoint(sketch, "E243.visualSharp", {"position": v(175.34, -466.25) * mm});
            skArc(sketch, "E243.filletArc", {"start": v(175.2, -465.4) * mm, "mid": v(175.54, -466) * mm, "end": v(176.2, -466.25) * mm});
            skLineSegment(sketch, "E244", {"start": v(236.73, -459.93) * mm, "end": v(247.92, -449.94) * mm});
            skLineSegment(sketch, "E245", {"start": v(247.92, -449.94) * mm, "end": v(252.85, -447.72) * mm});
            skLineSegment(sketch, "E246", {"start": v(254.92, -443.88) * mm, "end": v(242.02, -434.69) * mm});
            skLineSegment(sketch, "E247", {"start": v(242.02, -434.69) * mm, "end": v(233.61, -430.9) * mm});
            skLineSegment(sketch, "E248", {"start": v(230.81, -431.19) * mm, "end": v(216.25, -435.34) * mm});
            skLineSegment(sketch, "E249", {"start": v(216.25, -435.34) * mm, "end": v(200.5, -437.75) * mm});
            skLineSegment(sketch, "E250", {"start": v(200.5, -437.75) * mm, "end": v(199.84, -437.79) * mm});
            skLineSegment(sketch, "E251", {"start": v(166.54, -439.45) * mm, "end": v(163.67, -437.88) * mm});
            skLineSegment(sketch, "E252", {"start": v(163.67, -437.88) * mm, "end": v(158.84, -437.5) * mm});
            skPoint(sketch, "E253", {"position": v(157.06, -445.1) * mm});
            skLineSegment(sketch, "E254", {"start": v(164.36, -459.39) * mm, "end": v(164.36, -470.88) * mm});
            skLineSegment(sketch, "E255", {"start": v(164.36, -470.88) * mm, "end": v(164.93, -474.21) * mm});
            skLineSegment(sketch, "E256", {"start": v(164.93, -474.21) * mm, "end": v(166.6, -477.75) * mm});
            skLineSegment(sketch, "E257", {"start": v(166.6, -477.75) * mm, "end": v(168.75, -480.43) * mm});
            skLineSegment(sketch, "E258", {"start": v(168.75, -480.43) * mm, "end": v(172.54, -482.74) * mm});
            skLineSegment(sketch, "E259", {"start": v(175.19, -482.43) * mm, "end": v(175.89, -481.62) * mm});
            skLineSegment(sketch, "E260", {"start": v(175.89, -481.62) * mm, "end": v(176.33, -479.75) * mm});
            skLineSegment(sketch, "E261", {"start": v(176.33, -479.75) * mm, "end": v(176.29, -476.55) * mm});
            skLineSegment(sketch, "E262", {"start": v(177.2, -475.54) * mm, "end": v(204.4, -472.96) * mm});
            skLineSegment(sketch, "E263", {"start": v(204.4, -472.96) * mm, "end": v(235.12, -472.5) * mm});
            skLineSegment(sketch, "E264", {"start": v(237.2, -462.28) * mm, "end": v(240.12, -467.07) * mm});
            skArc(sketch, "E265", {"start": v(164.36, -459.39) * mm, "mid": v(161.74, -451.72) * mm, "end": v(157.06, -445.1) * mm});
            skArc(sketch, "E266", {"start": v(158.84, -437.5) * mm, "mid": v(155.42, -440.7) * mm, "end": v(157.06, -445.1) * mm});
            skArc(sketch, "E267", {"start": v(235.12, -472.5) * mm, "mid": v(238.63, -471.08) * mm, "end": v(240.27, -467.67) * mm});
            skArc(sketch, "E268", {"start": v(252.85, -447.72) * mm, "mid": v(255.57, -446.71) * mm, "end": v(254.92, -443.88) * mm});
            skArc(sketch, "E269", {"start": v(233.61, -430.9) * mm, "mid": v(232.2, -430.92) * mm, "end": v(230.81, -431.19) * mm});
            skLineSegment(sketch, "E270", {"start": v(237.2, -462.28) * mm, "end": v(236.54, -461.2) * mm});
            skPoint(sketch, "E271.visualSharp", {"position": v(236.1, -460.48) * mm});
            skArc(sketch, "E271.filletArc", {"start": v(236.73, -459.93) * mm, "mid": v(236.4, -460.53) * mm, "end": v(236.54, -461.2) * mm});
            skPoint(sketch, "E272.visualSharp", {"position": v(240.28, -467.33) * mm});
            skArc(sketch, "E272.filletArc", {"start": v(240.27, -467.67) * mm, "mid": v(240.24, -467.36) * mm, "end": v(240.12, -467.07) * mm});
            skPoint(sketch, "E273.visualSharp", {"position": v(224.58, -460.1) * mm});
            skArc(sketch, "E273.filletArc", {"start": v(224.33, -460.25) * mm, "mid": v(224.56, -460.08) * mm, "end": v(224.72, -459.86) * mm});
            skPoint(sketch, "E274.visualSharp", {"position": v(227.33, -455.15) * mm});
            skArc(sketch, "E274.filletArc", {"start": v(227.22, -455.33) * mm, "mid": v(227.3, -455.14) * mm, "end": v(227.35, -454.93) * mm});
            skPoint(sketch, "E275.visualSharp", {"position": v(217.53, -464.03) * mm});
            skArc(sketch, "E275.filletArc", {"start": v(217.36, -464.05) * mm, "mid": v(217.53, -464.01) * mm, "end": v(217.68, -463.94) * mm});
            skPoint(sketch, "E276.visualSharp", {"position": v(203.68, -466.25) * mm});
            skArc(sketch, "E276.filletArc", {"start": v(203.6, -466.25) * mm, "mid": v(203.68, -466.24) * mm, "end": v(203.76, -466.23) * mm});
            skPoint(sketch, "E277.visualSharp", {"position": v(176.27, -475.63) * mm});
            skArc(sketch, "E277.filletArc", {"start": v(177.2, -475.54) * mm, "mid": v(176.54, -475.87) * mm, "end": v(176.29, -476.55) * mm});
            skArc(sketch, "E278", {"start": v(172.54, -482.74) * mm, "mid": v(173.92, -483.1) * mm, "end": v(175.19, -482.43) * mm});
            skLineSegment(sketch, "E279", {"start": v(-248.97, -71.8) * mm, "end": v(-245.42, -80.96) * mm});
            skLineSegment(sketch, "E280", {"start": v(-245.31, -81.16) * mm, "end": v(-234.14, -97.7) * mm});
            skLineSegment(sketch, "E281", {"start": v(-228.24, -97.1) * mm, "end": v(-223.99, -93.86) * mm});
            skLineSegment(sketch, "E282", {"start": v(-223.22, -87.66) * mm, "end": v(-223.6, -93.13) * mm});
            skLineSegment(sketch, "E283", {"start": v(-223.5, -86.9) * mm, "end": v(-236, -74.17) * mm});
            skLineSegment(sketch, "E284", {"start": v(-236.29, -73.97) * mm, "end": v(-242.72, -70.98) * mm});
            skLineSegment(sketch, "E285", {"start": v(-243.05, -70.9) * mm, "end": v(-247.94, -70.45) * mm});
            skLineSegment(sketch, "E286", {"start": v(-199.43, -79.86) * mm, "end": v(-199.71, -86.53) * mm});
            skLineSegment(sketch, "E287", {"start": v(-199.56, -87.1) * mm, "end": v(-195.39, -93.87) * mm});
            skLineSegment(sketch, "E288", {"start": v(-194.57, -94.34) * mm, "end": v(-188.7, -94.54) * mm});
            skLineSegment(sketch, "E289", {"start": v(-187.83, -94.09) * mm, "end": v(-186.8, -92.53) * mm});
            skLineSegment(sketch, "E290", {"start": v(-186.29, -92.13) * mm, "end": v(-159, -82.86) * mm});
            skLineSegment(sketch, "E291", {"start": v(-158.69, -82.8) * mm, "end": v(-149.03, -82.65) * mm});
            skLineSegment(sketch, "E292", {"start": v(-148.6, -82.74) * mm, "end": v(-147.7, -83.14) * mm});
            skLineSegment(sketch, "E293", {"start": v(-147.27, -83.22) * mm, "end": v(-142.25, -83.14) * mm});
            skLineSegment(sketch, "E294", {"start": v(-141.86, -83.05) * mm, "end": v(-138.27, -81.45) * mm});
            skLineSegment(sketch, "E295", {"start": v(-137.68, -80.57) * mm, "end": v(-137.61, -78.35) * mm});
            skLineSegment(sketch, "E296", {"start": v(-137.68, -77.96) * mm, "end": v(-138.53, -75.73) * mm});
            skLineSegment(sketch, "E297", {"start": v(-138.84, -75.3) * mm, "end": v(-146.17, -69.52) * mm});
            skLineSegment(sketch, "E298", {"start": v(-197.76, -79.17) * mm, "end": v(-196.6, -80.22) * mm});
            skLineSegment(sketch, "E299", {"start": v(-192.03, -80.12) * mm, "end": v(-164.36, -71.51) * mm});
            skLineSegment(sketch, "E300", {"start": v(-164.17, -71.47) * mm, "end": v(-156.2, -70.64) * mm});
            skLineSegment(sketch, "E301", {"start": v(-155.7, -70.45) * mm, "end": v(-152.5, -68.1) * mm});
            skLineSegment(sketch, "E302", {"start": v(-151.9, -67.9) * mm, "end": v(-147.53, -67.97) * mm});
            skLineSegment(sketch, "E303", {"start": v(-146.56, -68.8) * mm, "end": v(-146.54, -68.9) * mm});
            skArc(sketch, "E304", {"start": v(-196.6, -80.22) * mm, "mid": v(-194.3, -80.5) * mm, "end": v(-192.03, -80.12) * mm});
            skPoint(sketch, "E305.visualSharp", {"position": v(-199.34, -77.73) * mm});
            skArc(sketch, "E305.filletArc", {"start": v(-197.76, -79.17) * mm, "mid": v(-198.81, -78.98) * mm, "end": v(-199.43, -79.86) * mm});
            skPoint(sketch, "E306.visualSharp", {"position": v(-199.72, -86.83) * mm});
            skArc(sketch, "E306.filletArc", {"start": v(-199.71, -86.53) * mm, "mid": v(-199.68, -86.82) * mm, "end": v(-199.56, -87.1) * mm});
            skPoint(sketch, "E307.visualSharp", {"position": v(-195.1, -94.32) * mm});
            skArc(sketch, "E307.filletArc", {"start": v(-195.39, -93.87) * mm, "mid": v(-195.04, -94.2) * mm, "end": v(-194.57, -94.34) * mm});
            skPoint(sketch, "E308.visualSharp", {"position": v(-188.13, -94.55) * mm});
            skArc(sketch, "E308.filletArc", {"start": v(-188.7, -94.54) * mm, "mid": v(-188.2, -94.42) * mm, "end": v(-187.83, -94.09) * mm});
            skPoint(sketch, "E309.visualSharp", {"position": v(-186.6, -92.24) * mm});
            skArc(sketch, "E309.filletArc", {"start": v(-186.29, -92.13) * mm, "mid": v(-186.57, -92.3) * mm, "end": v(-186.8, -92.53) * mm});
            skPoint(sketch, "E310.visualSharp", {"position": v(-164.27, -71.48) * mm});
            skArc(sketch, "E310.filletArc", {"start": v(-164.17, -71.47) * mm, "mid": v(-164.27, -71.49) * mm, "end": v(-164.36, -71.51) * mm});
            skPoint(sketch, "E311.visualSharp", {"position": v(-155.92, -70.6) * mm});
            skArc(sketch, "E311.filletArc", {"start": v(-156.2, -70.64) * mm, "mid": v(-155.93, -70.57) * mm, "end": v(-155.7, -70.45) * mm});
            skPoint(sketch, "E312.visualSharp", {"position": v(-152.23, -67.89) * mm});
            skArc(sketch, "E312.filletArc", {"start": v(-151.9, -67.9) * mm, "mid": v(-152.22, -67.94) * mm, "end": v(-152.5, -68.1) * mm});
            skPoint(sketch, "E313.visualSharp", {"position": v(-146.7, -67.99) * mm});
            skArc(sketch, "E313.filletArc", {"start": v(-146.56, -68.8) * mm, "mid": v(-146.9, -68.21) * mm, "end": v(-147.53, -67.97) * mm});
            skPoint(sketch, "E314.visualSharp", {"position": v(-146.48, -69.28) * mm});
            skArc(sketch, "E314.filletArc", {"start": v(-146.54, -68.9) * mm, "mid": v(-146.41, -69.25) * mm, "end": v(-146.17, -69.52) * mm});
            skPoint(sketch, "E315.visualSharp", {"position": v(-138.62, -75.47) * mm});
            skArc(sketch, "E315.filletArc", {"start": v(-138.53, -75.73) * mm, "mid": v(-138.65, -75.5) * mm, "end": v(-138.84, -75.3) * mm});
            skPoint(sketch, "E316.visualSharp", {"position": v(-137.6, -78.15) * mm});
            skArc(sketch, "E316.filletArc", {"start": v(-137.61, -78.35) * mm, "mid": v(-137.63, -78.15) * mm, "end": v(-137.68, -77.96) * mm});
            skPoint(sketch, "E317.visualSharp", {"position": v(-137.7, -81.2) * mm});
            skArc(sketch, "E317.filletArc", {"start": v(-138.27, -81.45) * mm, "mid": v(-137.85, -81.1) * mm, "end": v(-137.68, -80.57) * mm});
            skPoint(sketch, "E318.visualSharp", {"position": v(-142.04, -83.14) * mm});
            skArc(sketch, "E318.filletArc", {"start": v(-142.25, -83.14) * mm, "mid": v(-142.05, -83.12) * mm, "end": v(-141.86, -83.05) * mm});
            skPoint(sketch, "E319.visualSharp", {"position": v(-147.5, -83.23) * mm});
            skArc(sketch, "E319.filletArc", {"start": v(-147.7, -83.14) * mm, "mid": v(-147.49, -83.2) * mm, "end": v(-147.27, -83.22) * mm});
            skPoint(sketch, "E320.visualSharp", {"position": v(-148.8, -82.65) * mm});
            skArc(sketch, "E320.filletArc", {"start": v(-148.6, -82.74) * mm, "mid": v(-148.81, -82.67) * mm, "end": v(-149.03, -82.65) * mm});
            skPoint(sketch, "E321.visualSharp", {"position": v(-158.84, -82.8) * mm});
            skArc(sketch, "E321.filletArc", {"start": v(-158.69, -82.8) * mm, "mid": v(-158.84, -82.82) * mm, "end": v(-159, -82.86) * mm});
            skPoint(sketch, "E322.visualSharp", {"position": v(-223.63, -93.59) * mm});
            skArc(sketch, "E322.filletArc", {"start": v(-223.99, -93.86) * mm, "mid": v(-223.71, -93.54) * mm, "end": v(-223.6, -93.13) * mm});
            skPoint(sketch, "E323.visualSharp", {"position": v(-223.19, -87.22) * mm});
            skArc(sketch, "E323.filletArc", {"start": v(-223.22, -87.66) * mm, "mid": v(-223.28, -87.25) * mm, "end": v(-223.5, -86.9) * mm});
            skPoint(sketch, "E324.visualSharp", {"position": v(-236.12, -74.04) * mm});
            skArc(sketch, "E324.filletArc", {"start": v(-236, -74.17) * mm, "mid": v(-236.13, -74.06) * mm, "end": v(-236.29, -73.97) * mm});
            skPoint(sketch, "E325.visualSharp", {"position": v(-242.88, -70.91) * mm});
            skArc(sketch, "E325.filletArc", {"start": v(-242.72, -70.98) * mm, "mid": v(-242.88, -70.93) * mm, "end": v(-243.05, -70.9) * mm});
            skPoint(sketch, "E326.visualSharp", {"position": v(-249.55, -70.3) * mm});
            skArc(sketch, "E326.filletArc", {"start": v(-247.94, -70.45) * mm, "mid": v(-248.83, -70.84) * mm, "end": v(-248.97, -71.8) * mm});
            skPoint(sketch, "E327.visualSharp", {"position": v(-245.38, -81.07) * mm});
            skArc(sketch, "E327.filletArc", {"start": v(-245.42, -80.96) * mm, "mid": v(-245.37, -81.06) * mm, "end": v(-245.31, -81.16) * mm});
            skArc(sketch, "E328", {"start": v(-233.6, -98.1) * mm, "mid": v(-230.8, -98.24) * mm, "end": v(-228.24, -97.1) * mm});
            skPoint(sketch, "E329.visualSharp", {"position": v(-233.95, -97.98) * mm});
            skArc(sketch, "E329.filletArc", {"start": v(-234.14, -97.7) * mm, "mid": v(-233.9, -97.94) * mm, "end": v(-233.6, -98.1) * mm});
            skLineSegment(sketch, "E330", {"start": v(-187.02, -120.66) * mm, "end": v(-187.02, -131.3) * mm});
            skLineSegment(sketch, "E331", {"start": v(-185.61, -132.2) * mm, "end": v(-171.3, -125.78) * mm});
            skLineSegment(sketch, "E332", {"start": v(-168.35, -124.46) * mm, "end": v(-162.79, -123.37) * mm});
            skLineSegment(sketch, "E333", {"start": v(-161.98, -122.46) * mm, "end": v(-161.04, -108.69) * mm});
            skLineSegment(sketch, "E334", {"start": v(-161.06, -108.41) * mm, "end": v(-161.3, -107.23) * mm});
            skLineSegment(sketch, "E335", {"start": v(-162.77, -106.56) * mm, "end": v(-172.2, -111.8) * mm});
            skLineSegment(sketch, "E336", {"start": v(-202.05, -106.47) * mm, "end": v(-200.27, -111.1) * mm});
            skLineSegment(sketch, "E337", {"start": v(-200.2, -111.47) * mm, "end": v(-200.2, -127.03) * mm});
            skLineSegment(sketch, "E338", {"start": v(-200.26, -127.37) * mm, "end": v(-203.1, -135.16) * mm});
            skLineSegment(sketch, "E339", {"start": v(-202.76, -136.3) * mm, "end": v(-200.06, -138.3) * mm});
            skLineSegment(sketch, "E340", {"start": v(-199.65, -139.1) * mm, "end": v(-199.65, -140.18) * mm});
            skLineSegment(sketch, "E341", {"start": v(-199.44, -140.8) * mm, "end": v(-197.08, -143.83) * mm});
            skLineSegment(sketch, "E342", {"start": v(-196.26, -144.22) * mm, "end": v(-191.77, -144.1) * mm});
            skLineSegment(sketch, "E343", {"start": v(-191.13, -144.32) * mm, "end": v(-189.96, -145.23) * mm});
            skLineSegment(sketch, "E344", {"start": v(-188.94, -145.36) * mm, "end": v(-187.42, -144.69) * mm});
            skLineSegment(sketch, "E345", {"start": v(-186.88, -144.09) * mm, "end": v(-186.49, -142.9) * mm});
            skLineSegment(sketch, "E346", {"start": v(-185.88, -142.28) * mm, "end": v(-167.8, -135.64) * mm});
            skLineSegment(sketch, "E347", {"start": v(-167.54, -135.49) * mm, "end": v(-164.97, -133.5) * mm});
            skLineSegment(sketch, "E348", {"start": v(-163.44, -133.89) * mm, "end": v(-161.76, -137.78) * mm});
            skLineSegment(sketch, "E349", {"start": v(-157.14, -143.14) * mm, "end": v(-147.97, -143.14) * mm});
            skLineSegment(sketch, "E350", {"start": v(-147.04, -142.5) * mm, "end": v(-145.15, -137.66) * mm});
            skLineSegment(sketch, "E351", {"start": v(-145.09, -137.38) * mm, "end": v(-143.03, -113.95) * mm});
            skLineSegment(sketch, "E352", {"start": v(-142.94, -113.6) * mm, "end": v(-140.8, -109.2) * mm});
            skLineSegment(sketch, "E353", {"start": v(-140.64, -109.15) * mm, "end": v(-140.16, -109.38) * mm});
            skLineSegment(sketch, "E354", {"start": v(-138.83, -108.91) * mm, "end": v(-138.27, -107.77) * mm});
            skLineSegment(sketch, "E355", {"start": v(-138.27, -106.9) * mm, "end": v(-139.69, -103.88) * mm});
            skLineSegment(sketch, "E356", {"start": v(-140.1, -103.43) * mm, "end": v(-150.95, -97.44) * mm});
            skLineSegment(sketch, "E357", {"start": v(-158.7, -97.51) * mm, "end": v(-173.92, -103.84) * mm});
            skLineSegment(sketch, "E358", {"start": v(-188.61, -108.87) * mm, "end": v(-188.62, -108.84) * mm});
            skLineSegment(sketch, "E359", {"start": v(-189.02, -108.38) * mm, "end": v(-195.2, -104.6) * mm});
            skLineSegment(sketch, "E360", {"start": v(-195.72, -104.44) * mm, "end": v(-200.58, -104.44) * mm});
            skLineSegment(sketch, "E361", {"start": v(-201.36, -104.82) * mm, "end": v(-201.9, -105.48) * mm});
            skArc(sketch, "E362", {"start": v(-150.95, -97.44) * mm, "mid": v(-154.84, -96.72) * mm, "end": v(-158.7, -97.51) * mm});
            skArc(sketch, "E363", {"start": v(-161.76, -137.78) * mm, "mid": v(-160.68, -141.52) * mm, "end": v(-157.14, -143.14) * mm});
            skPoint(sketch, "E364.visualSharp", {"position": v(-202.26, -105.93) * mm});
            skArc(sketch, "E364.filletArc", {"start": v(-201.9, -105.48) * mm, "mid": v(-202.1, -105.95) * mm, "end": v(-202.05, -106.47) * mm});
            skPoint(sketch, "E365.visualSharp", {"position": v(-201.06, -104.44) * mm});
            skArc(sketch, "E365.filletArc", {"start": v(-200.58, -104.44) * mm, "mid": v(-201.02, -104.54) * mm, "end": v(-201.36, -104.82) * mm});
            skPoint(sketch, "E366.visualSharp", {"position": v(-195.43, -104.44) * mm});
            skArc(sketch, "E366.filletArc", {"start": v(-195.2, -104.6) * mm, "mid": v(-195.44, -104.48) * mm, "end": v(-195.72, -104.44) * mm});
            skPoint(sketch, "E367.visualSharp", {"position": v(-188.75, -108.54) * mm});
            skArc(sketch, "E367.filletArc", {"start": v(-188.62, -108.84) * mm, "mid": v(-188.79, -108.58) * mm, "end": v(-189.02, -108.38) * mm});
            skPoint(sketch, "E368.visualSharp", {"position": v(-188.23, -109.8) * mm});
            skArc(sketch, "E368.filletArc", {"start": v(-188.61, -108.87) * mm, "mid": v(-188.07, -109.41) * mm, "end": v(-187.3, -109.41) * mm});
            skPoint(sketch, "E369.visualSharp", {"position": v(-139.82, -103.58) * mm});
            skArc(sketch, "E369.filletArc", {"start": v(-139.69, -103.88) * mm, "mid": v(-139.86, -103.62) * mm, "end": v(-140.1, -103.43) * mm});
            skPoint(sketch, "E370.visualSharp", {"position": v(-138.06, -107.34) * mm});
            skArc(sketch, "E370.filletArc", {"start": v(-138.27, -107.77) * mm, "mid": v(-138.17, -107.34) * mm, "end": v(-138.27, -106.9) * mm});
            skPoint(sketch, "E371.visualSharp", {"position": v(-139.26, -109.81) * mm});
            skArc(sketch, "E371.filletArc", {"start": v(-140.16, -109.38) * mm, "mid": v(-139.4, -109.42) * mm, "end": v(-138.83, -108.91) * mm});
            skPoint(sketch, "E372.visualSharp", {"position": v(-140.75, -109.1) * mm});
            skArc(sketch, "E372.filletArc", {"start": v(-140.64, -109.15) * mm, "mid": v(-140.73, -109.14) * mm, "end": v(-140.8, -109.2) * mm});
            skPoint(sketch, "E373.visualSharp", {"position": v(-143.02, -113.77) * mm});
            skArc(sketch, "E373.filletArc", {"start": v(-142.94, -113.6) * mm, "mid": v(-143, -113.77) * mm, "end": v(-143.03, -113.95) * mm});
            skPoint(sketch, "E374.visualSharp", {"position": v(-145.1, -137.53) * mm});
            skArc(sketch, "E374.filletArc", {"start": v(-145.15, -137.66) * mm, "mid": v(-145.11, -137.52) * mm, "end": v(-145.09, -137.38) * mm});
            skPoint(sketch, "E375.visualSharp", {"position": v(-147.28, -143.14) * mm});
            skArc(sketch, "E375.filletArc", {"start": v(-147.97, -143.14) * mm, "mid": v(-147.4, -142.97) * mm, "end": v(-147.04, -142.5) * mm});
            skPoint(sketch, "E376.visualSharp", {"position": v(-163.96, -132.7) * mm});
            skArc(sketch, "E376.filletArc", {"start": v(-163.44, -133.89) * mm, "mid": v(-164.11, -133.31) * mm, "end": v(-164.97, -133.5) * mm});
            skPoint(sketch, "E377.visualSharp", {"position": v(-167.66, -135.58) * mm});
            skArc(sketch, "E377.filletArc", {"start": v(-167.8, -135.64) * mm, "mid": v(-167.67, -135.57) * mm, "end": v(-167.54, -135.49) * mm});
            skPoint(sketch, "E378.visualSharp", {"position": v(-186.33, -142.45) * mm});
            skArc(sketch, "E378.filletArc", {"start": v(-185.88, -142.28) * mm, "mid": v(-186.25, -142.52) * mm, "end": v(-186.49, -142.9) * mm});
            skPoint(sketch, "E379.visualSharp", {"position": v(-187.02, -144.5) * mm});
            skArc(sketch, "E379.filletArc", {"start": v(-187.42, -144.69) * mm, "mid": v(-187.09, -144.44) * mm, "end": v(-186.88, -144.09) * mm});
            skPoint(sketch, "E380.visualSharp", {"position": v(-189.5, -145.6) * mm});
            skArc(sketch, "E380.filletArc", {"start": v(-189.96, -145.23) * mm, "mid": v(-189.47, -145.44) * mm, "end": v(-188.94, -145.36) * mm});
            skPoint(sketch, "E381.visualSharp", {"position": v(-191.41, -144.1) * mm});
            skArc(sketch, "E381.filletArc", {"start": v(-191.13, -144.32) * mm, "mid": v(-191.43, -144.15) * mm, "end": v(-191.77, -144.1) * mm});
            skPoint(sketch, "E382.visualSharp", {"position": v(-196.77, -144.23) * mm});
            skArc(sketch, "E382.filletArc", {"start": v(-197.08, -143.83) * mm, "mid": v(-196.72, -144.12) * mm, "end": v(-196.26, -144.22) * mm});
            skPoint(sketch, "E383.visualSharp", {"position": v(-199.65, -140.53) * mm});
            skArc(sketch, "E383.filletArc", {"start": v(-199.65, -140.18) * mm, "mid": v(-199.6, -140.5) * mm, "end": v(-199.44, -140.8) * mm});
            skPoint(sketch, "E384.visualSharp", {"position": v(-199.65, -138.6) * mm});
            skArc(sketch, "E384.filletArc", {"start": v(-199.65, -139.1) * mm, "mid": v(-199.76, -138.66) * mm, "end": v(-200.06, -138.3) * mm});
            skPoint(sketch, "E385.visualSharp", {"position": v(-203.36, -135.86) * mm});
            skArc(sketch, "E385.filletArc", {"start": v(-203.1, -135.16) * mm, "mid": v(-203.12, -135.79) * mm, "end": v(-202.76, -136.3) * mm});
            skPoint(sketch, "E386.visualSharp", {"position": v(-200.2, -127.2) * mm});
            skArc(sketch, "E386.filletArc", {"start": v(-200.26, -127.37) * mm, "mid": v(-200.21, -127.2) * mm, "end": v(-200.2, -127.03) * mm});
            skPoint(sketch, "E387.visualSharp", {"position": v(-200.2, -111.28) * mm});
            skArc(sketch, "E387.filletArc", {"start": v(-200.2, -111.47) * mm, "mid": v(-200.22, -111.29) * mm, "end": v(-200.27, -111.1) * mm});
            skPoint(sketch, "E388.visualSharp", {"position": v(-187.02, -120.07) * mm});
            skArc(sketch, "E388.filletArc", {"start": v(-186.5, -119.78) * mm, "mid": v(-186.88, -120.15) * mm, "end": v(-187.02, -120.66) * mm});
            skPoint(sketch, "E389.visualSharp", {"position": v(-187.02, -132.84) * mm});
            skArc(sketch, "E389.filletArc", {"start": v(-187.02, -131.3) * mm, "mid": v(-186.56, -132.13) * mm, "end": v(-185.61, -132.2) * mm});
            skPoint(sketch, "E390.visualSharp", {"position": v(-162.03, -123.23) * mm});
            skArc(sketch, "E390.filletArc", {"start": v(-162.79, -123.37) * mm, "mid": v(-162.23, -123.05) * mm, "end": v(-161.98, -122.46) * mm});
            skPoint(sketch, "E391.visualSharp", {"position": v(-161.03, -108.55) * mm});
            skArc(sketch, "E391.filletArc", {"start": v(-161.04, -108.69) * mm, "mid": v(-161.04, -108.55) * mm, "end": v(-161.06, -108.41) * mm});
            skPoint(sketch, "E392.visualSharp", {"position": v(-161.58, -105.9) * mm});
            skArc(sketch, "E392.filletArc", {"start": v(-161.3, -107.23) * mm, "mid": v(-161.87, -106.52) * mm, "end": v(-162.77, -106.56) * mm});
            skLineSegment(sketch, "E393", {"start": v(-224.2, -148.67) * mm, "end": v(-224.2, -117.09) * mm});
            skLineSegment(sketch, "E394", {"start": v(-224.73, -116.2) * mm, "end": v(-236.4, -110.07) * mm});
            skLineSegment(sketch, "E395", {"start": v(-236.91, -110.42) * mm, "end": v(-236.82, -111.44) * mm});
            skLineSegment(sketch, "E396", {"start": v(-237.33, -112.4) * mm, "end": v(-261.6, -125.95) * mm});
            skLineSegment(sketch, "E397", {"start": v(-262.1, -126.69) * mm, "end": v(-263.04, -133.3) * mm});
            skLineSegment(sketch, "E398", {"start": v(-262.98, -133.8) * mm, "end": v(-260.44, -140.47) * mm});
            skLineSegment(sketch, "E399", {"start": v(-260.13, -140.9) * mm, "end": v(-258.5, -142.19) * mm});
            skLineSegment(sketch, "E400", {"start": v(-257.88, -142.4) * mm, "end": v(-253.92, -142.4) * mm});
            skLineSegment(sketch, "E401", {"start": v(-253.34, -142.23) * mm, "end": v(-243.14, -135.06) * mm});
            skLineSegment(sketch, "E402", {"start": v(-241.56, -135.86) * mm, "end": v(-241.4, -143.54) * mm});
            skLineSegment(sketch, "E403", {"start": v(-241.6, -144.16) * mm, "end": v(-279.8, -194.84) * mm});
            skLineSegment(sketch, "E404", {"start": v(-278.62, -196.36) * mm, "end": v(-269.47, -192.55) * mm});
            skLineSegment(sketch, "E405", {"start": v(-269.32, -192.47) * mm, "end": v(-256.81, -184.55) * mm});
            skLineSegment(sketch, "E406", {"start": v(-256.71, -184.48) * mm, "end": v(-246.97, -176.5) * mm});
            skLineSegment(sketch, "E407", {"start": v(-245.34, -177.35) * mm, "end": v(-247.7, -212.02) * mm});
            skLineSegment(sketch, "E408", {"start": v(-247.7, -212.18) * mm, "end": v(-247.18, -217.72) * mm});
            skLineSegment(sketch, "E409", {"start": v(-247.12, -217.99) * mm, "end": v(-239.63, -237.07) * mm});
            skLineSegment(sketch, "E410", {"start": v(-233.66, -236.25) * mm, "end": v(-228.5, -227.5) * mm});
            skLineSegment(sketch, "E411", {"start": v(-228.36, -227.03) * mm, "end": v(-226.19, -169.62) * mm});
            skLineSegment(sketch, "E412", {"start": v(-226.16, -169.43) * mm, "end": v(-224.32, -161.67) * mm});
            skLineSegment(sketch, "E413", {"start": v(-223.54, -161.52) * mm, "end": v(-220.81, -165.3) * mm});
            skLineSegment(sketch, "E414", {"start": v(-220.46, -165.62) * mm, "end": v(-218.86, -166.44) * mm});
            skLineSegment(sketch, "E415", {"start": v(-218.5, -166.54) * mm, "end": v(-212.6, -167.14) * mm});
            skLineSegment(sketch, "E416", {"start": v(-212.27, -167.12) * mm, "end": v(-210.66, -166.75) * mm});
            skLineSegment(sketch, "E417", {"start": v(-210.17, -166.47) * mm, "end": v(-208.33, -164.6) * mm});
            skLineSegment(sketch, "E418", {"start": v(-208.1, -164.18) * mm, "end": v(-207.72, -162.94) * mm});
            skLineSegment(sketch, "E419", {"start": v(-207.7, -162.42) * mm, "end": v(-208.7, -158.32) * mm});
            skLineSegment(sketch, "E420", {"start": v(-208.87, -157.94) * mm, "end": v(-211.06, -155.11) * mm});
            skLineSegment(sketch, "E421", {"start": v(-211.06, -155.11) * mm, "end": v(-223.6, -149.58) * mm});
            skPoint(sketch, "E422.visualSharp", {"position": v(-224.1, -160.74) * mm});
            skArc(sketch, "E422.filletArc", {"start": v(-223.54, -161.52) * mm, "mid": v(-223.98, -161.34) * mm, "end": v(-224.32, -161.67) * mm});
            skPoint(sketch, "E423.visualSharp", {"position": v(-207.64, -162.68) * mm});
            skArc(sketch, "E423.filletArc", {"start": v(-207.72, -162.94) * mm, "mid": v(-207.67, -162.68) * mm, "end": v(-207.7, -162.42) * mm});
            skPoint(sketch, "E424.visualSharp", {"position": v(-208.16, -164.42) * mm});
            skArc(sketch, "E424.filletArc", {"start": v(-208.33, -164.6) * mm, "mid": v(-208.19, -164.4) * mm, "end": v(-208.1, -164.18) * mm});
            skPoint(sketch, "E425.visualSharp", {"position": v(-210.37, -166.68) * mm});
            skArc(sketch, "E425.filletArc", {"start": v(-210.66, -166.75) * mm, "mid": v(-210.4, -166.64) * mm, "end": v(-210.17, -166.47) * mm});
            skPoint(sketch, "E426.visualSharp", {"position": v(-212.43, -167.15) * mm});
            skArc(sketch, "E426.filletArc", {"start": v(-212.6, -167.14) * mm, "mid": v(-212.43, -167.14) * mm, "end": v(-212.27, -167.12) * mm});
            skPoint(sketch, "E427.visualSharp", {"position": v(-218.7, -166.52) * mm});
            skArc(sketch, "E427.filletArc", {"start": v(-218.86, -166.44) * mm, "mid": v(-218.69, -166.5) * mm, "end": v(-218.5, -166.54) * mm});
            skPoint(sketch, "E428.visualSharp", {"position": v(-220.67, -165.5) * mm});
            skArc(sketch, "E428.filletArc", {"start": v(-220.81, -165.3) * mm, "mid": v(-220.65, -165.48) * mm, "end": v(-220.46, -165.62) * mm});
            skPoint(sketch, "E429.visualSharp", {"position": v(-208.74, -158.11) * mm});
            skArc(sketch, "E429.filletArc", {"start": v(-208.7, -158.32) * mm, "mid": v(-208.76, -158.12) * mm, "end": v(-208.87, -157.94) * mm});
            skPoint(sketch, "E430.visualSharp", {"position": v(-226.18, -169.52) * mm});
            skArc(sketch, "E430.filletArc", {"start": v(-226.16, -169.43) * mm, "mid": v(-226.18, -169.53) * mm, "end": v(-226.19, -169.62) * mm});
            skPoint(sketch, "E431.visualSharp", {"position": v(-228.37, -227.28) * mm});
            skArc(sketch, "E431.filletArc", {"start": v(-228.5, -227.5) * mm, "mid": v(-228.4, -227.27) * mm, "end": v(-228.36, -227.03) * mm});
            skPoint(sketch, "E432.visualSharp", {"position": v(-232.48, -234.25) * mm});
            skPoint(sketch, "E433.visualSharp", {"position": v(-240.05, -236) * mm});
            skPoint(sketch, "E434.visualSharp", {"position": v(-247.17, -217.86) * mm});
            skArc(sketch, "E434.filletArc", {"start": v(-247.18, -217.72) * mm, "mid": v(-247.16, -217.86) * mm, "end": v(-247.12, -217.99) * mm});
            skPoint(sketch, "E435.visualSharp", {"position": v(-247.7, -212.1) * mm});
            skArc(sketch, "E435.filletArc", {"start": v(-247.7, -212.02) * mm, "mid": v(-247.7, -212.1) * mm, "end": v(-247.7, -212.18) * mm});
            skPoint(sketch, "E436.visualSharp", {"position": v(-245.18, -175.04) * mm});
            skArc(sketch, "E436.filletArc", {"start": v(-245.34, -177.35) * mm, "mid": v(-245.88, -176.4) * mm, "end": v(-246.97, -176.5) * mm});
            skPoint(sketch, "E437.visualSharp", {"position": v(-256.76, -184.52) * mm});
            skArc(sketch, "E437.filletArc", {"start": v(-256.81, -184.55) * mm, "mid": v(-256.76, -184.52) * mm, "end": v(-256.71, -184.48) * mm});
            skPoint(sketch, "E438.visualSharp", {"position": v(-269.4, -192.52) * mm});
            skArc(sketch, "E438.filletArc", {"start": v(-269.47, -192.55) * mm, "mid": v(-269.4, -192.51) * mm, "end": v(-269.32, -192.47) * mm});
            skPoint(sketch, "E439.visualSharp", {"position": v(-282.03, -197.78) * mm});
            skArc(sketch, "E439.filletArc", {"start": v(-279.8, -194.84) * mm, "mid": v(-279.8, -196.05) * mm, "end": v(-278.62, -196.36) * mm});
            skPoint(sketch, "E440.visualSharp", {"position": v(-241.4, -143.88) * mm});
            skArc(sketch, "E440.filletArc", {"start": v(-241.6, -144.16) * mm, "mid": v(-241.45, -143.86) * mm, "end": v(-241.4, -143.54) * mm});
            skPoint(sketch, "E441.visualSharp", {"position": v(-224.2, -149.32) * mm});
            skArc(sketch, "E441.filletArc", {"start": v(-224.2, -148.67) * mm, "mid": v(-224.04, -149.21) * mm, "end": v(-223.6, -149.58) * mm});
            skPoint(sketch, "E442.visualSharp", {"position": v(-241.6, -133.99) * mm});
            skArc(sketch, "E442.filletArc", {"start": v(-241.56, -135.86) * mm, "mid": v(-242.1, -134.99) * mm, "end": v(-243.14, -135.06) * mm});
            skPoint(sketch, "E443.visualSharp", {"position": v(-253.6, -142.4) * mm});
            skArc(sketch, "E443.filletArc", {"start": v(-253.92, -142.4) * mm, "mid": v(-253.62, -142.36) * mm, "end": v(-253.34, -142.23) * mm});
            skPoint(sketch, "E444.visualSharp", {"position": v(-258.23, -142.4) * mm});
            skArc(sketch, "E444.filletArc", {"start": v(-258.5, -142.19) * mm, "mid": v(-258.21, -142.35) * mm, "end": v(-257.88, -142.4) * mm});
            skPoint(sketch, "E445.visualSharp", {"position": v(-260.34, -140.72) * mm});
            skArc(sketch, "E445.filletArc", {"start": v(-260.44, -140.47) * mm, "mid": v(-260.31, -140.7) * mm, "end": v(-260.13, -140.9) * mm});
            skPoint(sketch, "E446.visualSharp", {"position": v(-263.08, -133.56) * mm});
            skArc(sketch, "E446.filletArc", {"start": v(-263.04, -133.3) * mm, "mid": v(-263.04, -133.56) * mm, "end": v(-262.98, -133.8) * mm});
            skPoint(sketch, "E447.visualSharp", {"position": v(-262.02, -126.2) * mm});
            skArc(sketch, "E447.filletArc", {"start": v(-261.6, -125.95) * mm, "mid": v(-261.93, -126.26) * mm, "end": v(-262.1, -126.69) * mm});
            skPoint(sketch, "E448.visualSharp", {"position": v(-236.76, -112.09) * mm});
            skArc(sketch, "E448.filletArc", {"start": v(-237.33, -112.4) * mm, "mid": v(-236.93, -112) * mm, "end": v(-236.82, -111.44) * mm});
            skPoint(sketch, "E449.visualSharp", {"position": v(-236.97, -109.77) * mm});
            skArc(sketch, "E449.filletArc", {"start": v(-236.4, -110.07) * mm, "mid": v(-236.76, -110.1) * mm, "end": v(-236.91, -110.42) * mm});
            skPoint(sketch, "E450.visualSharp", {"position": v(-224.2, -116.48) * mm});
            skArc(sketch, "E450.filletArc", {"start": v(-224.2, -117.09) * mm, "mid": v(-224.34, -116.57) * mm, "end": v(-224.73, -116.2) * mm});
            skLineSegment(sketch, "E451", {"start": v(-136.23, -167.04) * mm, "end": v(-136.23, -179.08) * mm});
            skLineSegment(sketch, "E452", {"start": v(-136.24, -179.26) * mm, "end": v(-139.93, -200.15) * mm});
            skLineSegment(sketch, "E453", {"start": v(-139.98, -200.33) * mm, "end": v(-144.18, -211.26) * mm});
            skLineSegment(sketch, "E454", {"start": v(-144.88, -211.87) * mm, "end": v(-148.76, -212.8) * mm});
            skLineSegment(sketch, "E455", {"start": v(-149.07, -212.83) * mm, "end": v(-155.56, -212.28) * mm});
            skLineSegment(sketch, "E456", {"start": v(-155.64, -211.3) * mm, "end": v(-154.25, -210.95) * mm});
            skLineSegment(sketch, "E457", {"start": v(-153.5, -209.93) * mm, "end": v(-153.65, -206.67) * mm});
            skLineSegment(sketch, "E458", {"start": v(-154.11, -205.87) * mm, "end": v(-159.31, -202.6) * mm});
            skLineSegment(sketch, "E459", {"start": v(-159.84, -202.45) * mm, "end": v(-164, -202.45) * mm});
            skLineSegment(sketch, "E460", {"start": v(-165, -201.45) * mm, "end": v(-164.94, -190.53) * mm});
            skLineSegment(sketch, "E461", {"start": v(-164.17, -189.56) * mm, "end": v(-153.6, -187.08) * mm});
            skLineSegment(sketch, "E462", {"start": v(-153.22, -186.9) * mm, "end": v(-150.72, -185) * mm});
            skLineSegment(sketch, "E463", {"start": v(-150.65, -183.46) * mm, "end": v(-153.35, -181.03) * mm});
            skLineSegment(sketch, "E464", {"start": v(-154.02, -180.77) * mm, "end": v(-155.17, -180.77) * mm});
            skLineSegment(sketch, "E465", {"start": v(-155.87, -180.48) * mm, "end": v(-157.79, -178.61) * mm});
            skLineSegment(sketch, "E466", {"start": v(-158.49, -178.33) * mm, "end": v(-163.36, -178.33) * mm});
            skLineSegment(sketch, "E467", {"start": v(-164, -178.55) * mm, "end": v(-164.8, -179.22) * mm});
            skLineSegment(sketch, "E468", {"start": v(-166.43, -178.6) * mm, "end": v(-167.48, -172) * mm});
            skLineSegment(sketch, "E469", {"start": v(-167.81, -171.41) * mm, "end": v(-168.52, -170.8) * mm});
            skLineSegment(sketch, "E470", {"start": v(-168.1, -169.07) * mm, "end": v(-150.7, -164.63) * mm});
            skLineSegment(sketch, "E471", {"start": v(-150.45, -164.6) * mm, "end": v(-148.44, -164.6) * mm});
            skLineSegment(sketch, "E472", {"start": v(-143, -164.66) * mm, "end": v(-137, -166.07) * mm});
            skPoint(sketch, "E473.visualSharp", {"position": v(-167.54, -171.65) * mm});
            skArc(sketch, "E473.filletArc", {"start": v(-167.48, -172) * mm, "mid": v(-167.6, -171.68) * mm, "end": v(-167.81, -171.41) * mm});
            skPoint(sketch, "E474.visualSharp", {"position": v(-166.16, -180.33) * mm});
            skArc(sketch, "E474.filletArc", {"start": v(-166.43, -178.6) * mm, "mid": v(-165.8, -179.39) * mm, "end": v(-164.8, -179.22) * mm});
            skPoint(sketch, "E475.visualSharp", {"position": v(-163.71, -178.33) * mm});
            skArc(sketch, "E475.filletArc", {"start": v(-163.36, -178.33) * mm, "mid": v(-163.7, -178.39) * mm, "end": v(-164, -178.55) * mm});
            skPoint(sketch, "E476.visualSharp", {"position": v(-158.08, -178.33) * mm});
            skArc(sketch, "E476.filletArc", {"start": v(-157.79, -178.61) * mm, "mid": v(-158.11, -178.4) * mm, "end": v(-158.49, -178.33) * mm});
            skPoint(sketch, "E477.visualSharp", {"position": v(-155.58, -180.77) * mm});
            skArc(sketch, "E477.filletArc", {"start": v(-155.87, -180.48) * mm, "mid": v(-155.55, -180.7) * mm, "end": v(-155.17, -180.77) * mm});
            skPoint(sketch, "E478.visualSharp", {"position": v(-153.64, -180.77) * mm});
            skArc(sketch, "E478.filletArc", {"start": v(-153.35, -181.03) * mm, "mid": v(-153.66, -180.84) * mm, "end": v(-154.02, -180.77) * mm});
            skPoint(sketch, "E479.visualSharp", {"position": v(-149.76, -184.27) * mm});
            skArc(sketch, "E479.filletArc", {"start": v(-150.72, -185) * mm, "mid": v(-150.32, -184.25) * mm, "end": v(-150.65, -183.46) * mm});
            skPoint(sketch, "E480.visualSharp", {"position": v(-164.94, -189.74) * mm});
            skArc(sketch, "E480.filletArc", {"start": v(-164.17, -189.56) * mm, "mid": v(-164.72, -189.91) * mm, "end": v(-164.94, -190.53) * mm});
            skPoint(sketch, "E481.visualSharp", {"position": v(-153.39, -187.03) * mm});
            skArc(sketch, "E481.filletArc", {"start": v(-153.6, -187.08) * mm, "mid": v(-153.4, -187) * mm, "end": v(-153.22, -186.9) * mm});
            skPoint(sketch, "E482.visualSharp", {"position": v(-165, -202.45) * mm});
            skArc(sketch, "E482.filletArc", {"start": v(-165, -201.45) * mm, "mid": v(-164.7, -202.16) * mm, "end": v(-164, -202.45) * mm});
            skPoint(sketch, "E483.visualSharp", {"position": v(-159.55, -202.45) * mm});
            skArc(sketch, "E483.filletArc", {"start": v(-159.31, -202.6) * mm, "mid": v(-159.57, -202.49) * mm, "end": v(-159.84, -202.45) * mm});
            skPoint(sketch, "E484.visualSharp", {"position": v(-153.67, -206.14) * mm});
            skArc(sketch, "E484.filletArc", {"start": v(-153.65, -206.67) * mm, "mid": v(-153.78, -206.2) * mm, "end": v(-154.11, -205.87) * mm});
            skPoint(sketch, "E485.visualSharp", {"position": v(-153.46, -210.75) * mm});
            skArc(sketch, "E485.filletArc", {"start": v(-154.25, -210.95) * mm, "mid": v(-153.7, -210.58) * mm, "end": v(-153.5, -209.93) * mm});
            skPoint(sketch, "E486.visualSharp", {"position": v(-158.55, -212.03) * mm});
            skArc(sketch, "E486.filletArc", {"start": v(-155.64, -211.3) * mm, "mid": v(-156.02, -211.82) * mm, "end": v(-155.56, -212.28) * mm});
            skPoint(sketch, "E487.visualSharp", {"position": v(-148.91, -212.84) * mm});
            skArc(sketch, "E487.filletArc", {"start": v(-149.07, -212.83) * mm, "mid": v(-148.91, -212.83) * mm, "end": v(-148.76, -212.8) * mm});
            skPoint(sketch, "E488.visualSharp", {"position": v(-144.37, -211.75) * mm});
            skArc(sketch, "E488.filletArc", {"start": v(-144.88, -211.87) * mm, "mid": v(-144.45, -211.65) * mm, "end": v(-144.18, -211.26) * mm});
            skPoint(sketch, "E489.visualSharp", {"position": v(-139.94, -200.24) * mm});
            skArc(sketch, "E489.filletArc", {"start": v(-139.98, -200.33) * mm, "mid": v(-139.95, -200.24) * mm, "end": v(-139.93, -200.15) * mm});
            skPoint(sketch, "E490.visualSharp", {"position": v(-136.23, -179.17) * mm});
            skArc(sketch, "E490.filletArc", {"start": v(-136.24, -179.26) * mm, "mid": v(-136.23, -179.17) * mm, "end": v(-136.23, -179.08) * mm});
            skPoint(sketch, "E491.visualSharp", {"position": v(-136.23, -166.25) * mm});
            skArc(sketch, "E491.filletArc", {"start": v(-136.23, -167.04) * mm, "mid": v(-136.44, -166.42) * mm, "end": v(-137, -166.07) * mm});
            skPoint(sketch, "E492.visualSharp", {"position": v(-143.1, -164.63) * mm});
            skArc(sketch, "E492.filletArc", {"start": v(-143, -164.66) * mm, "mid": v(-143.1, -164.64) * mm, "end": v(-143.22, -164.63) * mm});
            skPoint(sketch, "E493.visualSharp", {"position": v(-150.58, -164.6) * mm});
            skArc(sketch, "E493.filletArc", {"start": v(-150.45, -164.6) * mm, "mid": v(-150.58, -164.6) * mm, "end": v(-150.7, -164.63) * mm});
            skPoint(sketch, "E494.visualSharp", {"position": v(-169.95, -169.54) * mm});
            skArc(sketch, "E494.filletArc", {"start": v(-168.1, -169.07) * mm, "mid": v(-168.83, -169.8) * mm, "end": v(-168.52, -170.8) * mm});
            skLineSegment(sketch, "E495", {"start": v(-180.42, -172.81) * mm, "end": v(-186.9, -175.3) * mm});
            skLineSegment(sketch, "E496", {"start": v(-199, -180.8) * mm, "end": v(-194.36, -203.54) * mm});
            skLineSegment(sketch, "E497", {"start": v(-194.14, -204) * mm, "end": v(-191.85, -206.66) * mm});
            skLineSegment(sketch, "E498", {"start": v(-191.61, -207.26) * mm, "end": v(-191.5, -209.38) * mm});
            skLineSegment(sketch, "E499", {"start": v(-191.05, -210.18) * mm, "end": v(-188.64, -211.71) * mm});
            skLineSegment(sketch, "E500", {"start": v(-187.73, -211.8) * mm, "end": v(-180.34, -208.86) * mm});
            skLineSegment(sketch, "E501", {"start": v(-179.72, -207.75) * mm, "end": v(-179.93, -206.66) * mm});
            skLineSegment(sketch, "E502", {"start": v(-179.7, -205.81) * mm, "end": v(-179.23, -205.28) * mm});
            skLineSegment(sketch, "E503", {"start": v(-178.98, -204.6) * mm, "end": v(-179.08, -200.02) * mm});
            skLineSegment(sketch, "E504", {"start": v(-180.66, -199.23) * mm, "end": v(-183.16, -201) * mm});
            skLineSegment(sketch, "E505", {"start": v(-183.73, -201.19) * mm, "end": v(-189.93, -201.27) * mm});
            skLineSegment(sketch, "E506", {"start": v(-190.49, -201.1) * mm, "end": v(-193.37, -199.23) * mm});
            skLineSegment(sketch, "E507", {"start": v(-193.82, -198.5) * mm, "end": v(-194.36, -193.19) * mm});
            skLineSegment(sketch, "E508", {"start": v(-193.27, -192.1) * mm, "end": v(-192.85, -192.13) * mm});
            skLineSegment(sketch, "E509", {"start": v(-192.65, -191.93) * mm, "end": v(-192.74, -191.03) * mm});
            skLineSegment(sketch, "E510", {"start": v(-191.49, -189.96) * mm, "end": v(-190.6, -190.2) * mm});
            skLineSegment(sketch, "E511", {"start": v(-189.9, -190.13) * mm, "end": v(-179.56, -185.17) * mm});
            skLineSegment(sketch, "E512", {"start": v(-179, -184.26) * mm, "end": v(-179.06, -173.74) * mm});
            skPoint(sketch, "E513.visualSharp", {"position": v(-179.07, -172.3) * mm});
            skArc(sketch, "E513.filletArc", {"start": v(-179.06, -173.74) * mm, "mid": v(-179.5, -172.92) * mm, "end": v(-180.42, -172.81) * mm});
            skPoint(sketch, "E514.visualSharp", {"position": v(-199.17, -179.97) * mm});
            skArc(sketch, "E514.filletArc", {"start": v(-198.37, -179.66) * mm, "mid": v(-198.9, -180.12) * mm, "end": v(-199, -180.8) * mm});
            skPoint(sketch, "E515.visualSharp", {"position": v(-194.31, -203.8) * mm});
            skArc(sketch, "E515.filletArc", {"start": v(-194.36, -203.54) * mm, "mid": v(-194.28, -203.78) * mm, "end": v(-194.14, -204) * mm});
            skPoint(sketch, "E516.visualSharp", {"position": v(-191.63, -206.92) * mm});
            skArc(sketch, "E516.filletArc", {"start": v(-191.61, -207.26) * mm, "mid": v(-191.68, -206.94) * mm, "end": v(-191.85, -206.66) * mm});
            skPoint(sketch, "E517.visualSharp", {"position": v(-191.48, -209.9) * mm});
            skArc(sketch, "E517.filletArc", {"start": v(-191.5, -209.38) * mm, "mid": v(-191.37, -209.84) * mm, "end": v(-191.05, -210.18) * mm});
            skPoint(sketch, "E518.visualSharp", {"position": v(-188.2, -211.99) * mm});
            skArc(sketch, "E518.filletArc", {"start": v(-188.64, -211.71) * mm, "mid": v(-188.2, -211.86) * mm, "end": v(-187.73, -211.8) * mm});
            skPoint(sketch, "E519.visualSharp", {"position": v(-179.57, -208.56) * mm});
            skArc(sketch, "E519.filletArc", {"start": v(-180.34, -208.86) * mm, "mid": v(-179.83, -208.42) * mm, "end": v(-179.72, -207.75) * mm});
            skPoint(sketch, "E520.visualSharp", {"position": v(-180.02, -206.18) * mm});
            skArc(sketch, "E520.filletArc", {"start": v(-179.7, -205.81) * mm, "mid": v(-179.91, -206.2) * mm, "end": v(-179.93, -206.66) * mm});
            skPoint(sketch, "E521.visualSharp", {"position": v(-178.98, -204.99) * mm});
            skArc(sketch, "E521.filletArc", {"start": v(-179.23, -205.28) * mm, "mid": v(-179.04, -204.96) * mm, "end": v(-178.98, -204.6) * mm});
            skPoint(sketch, "E522.visualSharp", {"position": v(-179.12, -198.14) * mm});
            skArc(sketch, "E522.filletArc", {"start": v(-179.08, -200.02) * mm, "mid": v(-179.63, -199.15) * mm, "end": v(-180.66, -199.23) * mm});
            skPoint(sketch, "E523.visualSharp", {"position": v(-183.42, -201.18) * mm});
            skArc(sketch, "E523.filletArc", {"start": v(-183.73, -201.19) * mm, "mid": v(-183.43, -201.14) * mm, "end": v(-183.16, -201) * mm});
            skPoint(sketch, "E524.visualSharp", {"position": v(-190.23, -201.27) * mm});
            skArc(sketch, "E524.filletArc", {"start": v(-190.49, -201.1) * mm, "mid": v(-190.22, -201.23) * mm, "end": v(-189.93, -201.27) * mm});
            skPoint(sketch, "E525.visualSharp", {"position": v(-193.78, -198.97) * mm});
            skArc(sketch, "E525.filletArc", {"start": v(-193.82, -198.5) * mm, "mid": v(-193.68, -198.91) * mm, "end": v(-193.37, -199.23) * mm});
            skPoint(sketch, "E526.visualSharp", {"position": v(-194.48, -191.98) * mm});
            skArc(sketch, "E526.filletArc", {"start": v(-193.27, -192.1) * mm, "mid": v(-194.08, -192.38) * mm, "end": v(-194.36, -193.19) * mm});
            skPoint(sketch, "E527.visualSharp", {"position": v(-192.9, -189.59) * mm});
            skArc(sketch, "E527.filletArc", {"start": v(-191.49, -189.96) * mm, "mid": v(-192.4, -190.16) * mm, "end": v(-192.74, -191.03) * mm});
            skPoint(sketch, "E528.visualSharp", {"position": v(-190.23, -190.3) * mm});
            skArc(sketch, "E528.filletArc", {"start": v(-190.6, -190.2) * mm, "mid": v(-190.24, -190.23) * mm, "end": v(-189.9, -190.13) * mm});
            skPoint(sketch, "E529.visualSharp", {"position": v(-179, -184.9) * mm});
            skArc(sketch, "E529.filletArc", {"start": v(-179.56, -185.17) * mm, "mid": v(-179.15, -184.8) * mm, "end": v(-179, -184.26) * mm});
            skPoint(sketch, "E530.visualSharp", {"position": v(-192.62, -192.15) * mm});
            skArc(sketch, "E530.filletArc", {"start": v(-192.85, -192.13) * mm, "mid": v(-192.7, -192.08) * mm, "end": v(-192.65, -191.93) * mm});
            skLineSegment(sketch, "E531", {"start": v(-200.03, -173.12) * mm, "end": v(-206.69, -168.64) * mm});
            skLineSegment(sketch, "E532", {"start": v(-207.16, -168.47) * mm, "end": v(-209.7, -168.25) * mm});
            skLineSegment(sketch, "E533", {"start": v(-210.65, -168.73) * mm, "end": v(-212, -170.98) * mm});
            skLineSegment(sketch, "E534", {"start": v(-212.13, -171.4) * mm, "end": v(-212.77, -178.23) * mm});
            skLineSegment(sketch, "E535", {"start": v(-212.78, -178.32) * mm, "end": v(-212.78, -190.82) * mm});
            skLineSegment(sketch, "E536", {"start": v(-212.77, -190.96) * mm, "end": v(-210.42, -207.35) * mm});
            skLineSegment(sketch, "E537", {"start": v(-210.38, -207.5) * mm, "end": v(-209.52, -210.6) * mm});
            skLineSegment(sketch, "E538", {"start": v(-209.3, -210.98) * mm, "end": v(-205.35, -215.44) * mm});
            skLineSegment(sketch, "E539", {"start": v(-205.35, -215.44) * mm, "end": v(-202.4, -216.7) * mm});
            skLineSegment(sketch, "E540", {"start": v(-202.4, -216.7) * mm, "end": v(-197.69, -216.35) * mm});
            skLineSegment(sketch, "E541", {"start": v(-196.61, -217.27) * mm, "end": v(-196.38, -220.43) * mm});
            skLineSegment(sketch, "E542", {"start": v(-195.12, -221.33) * mm, "end": v(-175.38, -216.02) * mm});
            skLineSegment(sketch, "E543", {"start": v(-174.66, -216.1) * mm, "end": v(-173.3, -216.82) * mm});
            skLineSegment(sketch, "E544", {"start": v(-172.68, -216.92) * mm, "end": v(-167.83, -216.18) * mm});
            skLineSegment(sketch, "E545", {"start": v(-167.3, -215.93) * mm, "end": v(-165.42, -214.2) * mm});
            skLineSegment(sketch, "E546", {"start": v(-164.47, -213.97) * mm, "end": v(-158.06, -215.82) * mm});
            skLineSegment(sketch, "E547", {"start": v(-158.06, -215.82) * mm, "end": v(-152.27, -219.08) * mm});
            skLineSegment(sketch, "E548", {"start": v(-152.27, -219.08) * mm, "end": v(-145.65, -225.15) * mm});
            skLineSegment(sketch, "E549", {"start": v(-145.65, -225.15) * mm, "end": v(-139.17, -228.57) * mm});
            skLineSegment(sketch, "E550", {"start": v(-139.17, -228.57) * mm, "end": v(-132.47, -228.65) * mm});
            skLineSegment(sketch, "E551", {"start": v(-132.47, -228.65) * mm, "end": v(-129.42, -227.16) * mm});
            skLineSegment(sketch, "E552", {"start": v(-129.42, -227.16) * mm, "end": v(-125.84, -223.74) * mm});
            skLineSegment(sketch, "E553", {"start": v(-125.84, -223.74) * mm, "end": v(-125.32, -220.83) * mm});
            skLineSegment(sketch, "E554", {"start": v(-125.32, -220.83) * mm, "end": v(-122.29, -215.06) * mm});
            skLineSegment(sketch, "E555", {"start": v(-122.29, -215.06) * mm, "end": v(-118.57, -199.13) * mm});
            skLineSegment(sketch, "E556", {"start": v(-118.57, -199.13) * mm, "end": v(-117.67, -187.82) * mm});
            skLineSegment(sketch, "E557", {"start": v(-117.67, -187.82) * mm, "end": v(-116.36, -166.16) * mm});
            skLineSegment(sketch, "E558", {"start": v(-116.75, -165.3) * mm, "end": v(-127.3, -157.16) * mm});
            skLineSegment(sketch, "E559", {"start": v(-127.92, -156.95) * mm, "end": v(-140.1, -157.04) * mm});
            skLineSegment(sketch, "E560", {"start": v(-140.19, -157.04) * mm, "end": v(-145.5, -157.53) * mm});
            skLineSegment(sketch, "E561", {"start": v(-152.78, -158.22) * mm, "end": v(-171.93, -163.34) * mm});
            skLineSegment(sketch, "E562", {"start": v(-172.01, -163.36) * mm, "end": v(-187.6, -169.04) * mm});
            skPoint(sketch, "E563.visualSharp", {"position": v(-152.7, -158.2) * mm});
            skArc(sketch, "E563.filletArc", {"start": v(-152.61, -158.19) * mm, "mid": v(-152.7, -158.2) * mm, "end": v(-152.78, -158.22) * mm});
            skPoint(sketch, "E564.visualSharp", {"position": v(-140.14, -157.04) * mm});
            skArc(sketch, "E564.filletArc", {"start": v(-140.1, -157.04) * mm, "mid": v(-140.14, -157.04) * mm, "end": v(-140.19, -157.04) * mm});
            skPoint(sketch, "E565.visualSharp", {"position": v(-127.57, -156.95) * mm});
            skArc(sketch, "E565.filletArc", {"start": v(-127.3, -157.16) * mm, "mid": v(-127.6, -157) * mm, "end": v(-127.92, -156.95) * mm});
            skPoint(sketch, "E566.visualSharp", {"position": v(-116.33, -165.63) * mm});
            skArc(sketch, "E566.filletArc", {"start": v(-116.36, -166.16) * mm, "mid": v(-116.45, -165.68) * mm, "end": v(-116.75, -165.3) * mm});
            skPoint(sketch, "E567.visualSharp", {"position": v(-171.97, -163.35) * mm});
            skArc(sketch, "E567.filletArc", {"start": v(-171.93, -163.34) * mm, "mid": v(-171.97, -163.35) * mm, "end": v(-172.01, -163.36) * mm});
            skPoint(sketch, "E568.visualSharp", {"position": v(-199.6, -173.4) * mm});
            skArc(sketch, "E568.filletArc", {"start": v(-200.03, -173.12) * mm, "mid": v(-199.6, -173.28) * mm, "end": v(-199.13, -173.23) * mm});
            skPoint(sketch, "E569.visualSharp", {"position": v(-206.9, -168.5) * mm});
            skArc(sketch, "E569.filletArc", {"start": v(-206.69, -168.64) * mm, "mid": v(-206.91, -168.52) * mm, "end": v(-207.16, -168.47) * mm});
            skPoint(sketch, "E570.visualSharp", {"position": v(-210.33, -168.2) * mm});
            skArc(sketch, "E570.filletArc", {"start": v(-209.7, -168.25) * mm, "mid": v(-210.24, -168.35) * mm, "end": v(-210.65, -168.73) * mm});
            skPoint(sketch, "E571.visualSharp", {"position": v(-212.11, -171.17) * mm});
            skArc(sketch, "E571.filletArc", {"start": v(-212, -170.98) * mm, "mid": v(-212.09, -171.18) * mm, "end": v(-212.13, -171.4) * mm});
            skPoint(sketch, "E572.visualSharp", {"position": v(-212.78, -178.27) * mm});
            skArc(sketch, "E572.filletArc", {"start": v(-212.77, -178.23) * mm, "mid": v(-212.78, -178.27) * mm, "end": v(-212.78, -178.32) * mm});
            skPoint(sketch, "E573.visualSharp", {"position": v(-212.78, -190.9) * mm});
            skArc(sketch, "E573.filletArc", {"start": v(-212.78, -190.82) * mm, "mid": v(-212.77, -190.9) * mm, "end": v(-212.77, -190.96) * mm});
            skPoint(sketch, "E574.visualSharp", {"position": v(-210.4, -207.43) * mm});
            skArc(sketch, "E574.filletArc", {"start": v(-210.42, -207.35) * mm, "mid": v(-210.4, -207.43) * mm, "end": v(-210.38, -207.5) * mm});
            skPoint(sketch, "E575.visualSharp", {"position": v(-209.46, -210.81) * mm});
            skArc(sketch, "E575.filletArc", {"start": v(-209.52, -210.6) * mm, "mid": v(-209.43, -210.8) * mm, "end": v(-209.3, -210.98) * mm});
            skPoint(sketch, "E576.visualSharp", {"position": v(-196.69, -216.28) * mm});
            skArc(sketch, "E576.filletArc", {"start": v(-196.61, -217.27) * mm, "mid": v(-196.96, -216.6) * mm, "end": v(-197.69, -216.35) * mm});
            skPoint(sketch, "E577.visualSharp", {"position": v(-196.28, -221.64) * mm});
            skArc(sketch, "E577.filletArc", {"start": v(-196.38, -220.43) * mm, "mid": v(-195.96, -221.18) * mm, "end": v(-195.12, -221.33) * mm});
            skPoint(sketch, "E578.visualSharp", {"position": v(-175, -215.92) * mm});
            skArc(sketch, "E578.filletArc", {"start": v(-174.66, -216.1) * mm, "mid": v(-175.01, -216) * mm, "end": v(-175.38, -216.02) * mm});
            skPoint(sketch, "E579.visualSharp", {"position": v(-173, -216.97) * mm});
            skArc(sketch, "E579.filletArc", {"start": v(-173.3, -216.82) * mm, "mid": v(-173, -216.92) * mm, "end": v(-172.68, -216.92) * mm});
            skPoint(sketch, "E580.visualSharp", {"position": v(-167.53, -216.13) * mm});
            skArc(sketch, "E580.filletArc", {"start": v(-167.83, -216.18) * mm, "mid": v(-167.55, -216.1) * mm, "end": v(-167.3, -215.93) * mm});
            skPoint(sketch, "E581.visualSharp", {"position": v(-165, -213.82) * mm});
            skArc(sketch, "E581.filletArc", {"start": v(-164.47, -213.97) * mm, "mid": v(-164.97, -213.96) * mm, "end": v(-165.42, -214.2) * mm});
            skLineSegment(sketch, "E582", {"start": v(-199.76, -342.99) * mm, "end": v(-183.55, -342.99) * mm});
            skLineSegment(sketch, "E583", {"start": v(-183.13, -342.9) * mm, "end": v(-163.94, -333.99) * mm});
            skLineSegment(sketch, "E584", {"start": v(-163.06, -334) * mm, "end": v(-149.63, -340.89) * mm});
            skLineSegment(sketch, "E585", {"start": v(-149.1, -341.93) * mm, "end": v(-150.02, -347.78) * mm});
            skLineSegment(sketch, "E586", {"start": v(-150.12, -348.09) * mm, "end": v(-159.5, -366.14) * mm});
            skLineSegment(sketch, "E587", {"start": v(-159.6, -366.6) * mm, "end": v(-159.6, -375.04) * mm});
            skLineSegment(sketch, "E588", {"start": v(-158.4, -376.02) * mm, "end": v(-141.05, -372.42) * mm});
            skLineSegment(sketch, "E589", {"start": v(-140.62, -372.43) * mm, "end": v(-132.79, -374.23) * mm});
            skLineSegment(sketch, "E590", {"start": v(-136.59, -381.23) * mm, "end": v(-176.47, -388.1) * mm});
            skLineSegment(sketch, "E591", {"start": v(-177.23, -389.45) * mm, "end": v(-174.9, -395.58) * mm});
            skLineSegment(sketch, "E592", {"start": v(-174.83, -395.93) * mm, "end": v(-174.83, -414.55) * mm});
            skLineSegment(sketch, "E593", {"start": v(-189.7, -459.55) * mm, "end": v(-197.85, -456.36) * mm});
            skLineSegment(sketch, "E594", {"start": v(-201.39, -462.03) * mm, "end": v(-194.14, -474.79) * mm});
            skLineSegment(sketch, "E595", {"start": v(-185.45, -454.6) * mm, "end": v(-185.45, -390.57) * mm});
            skLineSegment(sketch, "E596", {"start": v(-186.63, -389.59) * mm, "end": v(-210.75, -393.94) * mm});
            skLineSegment(sketch, "E597", {"start": v(-211.14, -393.93) * mm, "end": v(-219.13, -392.16) * mm});
            skLineSegment(sketch, "E598", {"start": v(-219.77, -390.66) * mm, "end": v(-216.15, -384.8) * mm});
            skLineSegment(sketch, "E599", {"start": v(-215.4, -384.34) * mm, "end": v(-186.02, -380.98) * mm});
            skLineSegment(sketch, "E600", {"start": v(-185.9, -380.97) * mm, "end": v(-173.16, -380.97) * mm});
            skLineSegment(sketch, "E601", {"start": v(-172.16, -379.99) * mm, "end": v(-172.02, -371.6) * mm});
            skLineSegment(sketch, "E602", {"start": v(-171.9, -371.14) * mm, "end": v(-161.9, -352.51) * mm});
            skLineSegment(sketch, "E603", {"start": v(-161.8, -351.84) * mm, "end": v(-162.92, -346.25) * mm});
            skLineSegment(sketch, "E604", {"start": v(-164.24, -345.5) * mm, "end": v(-182.46, -352.14) * mm});
            skLineSegment(sketch, "E605", {"start": v(-182.79, -352.2) * mm, "end": v(-200.61, -352.5) * mm});
            skArc(sketch, "E606", {"start": v(-199.76, -342.99) * mm, "mid": v(-205.47, -347.26) * mm, "end": v(-200.61, -352.5) * mm});
            skArc(sketch, "E607", {"start": v(-136.59, -381.23) * mm, "mid": v(-132.68, -379.88) * mm, "end": v(-131.25, -376) * mm});
            skArc(sketch, "E608", {"start": v(-193.56, -475.25) * mm, "mid": v(-180.7, -473) * mm, "end": v(-174.83, -461.32) * mm});
            skArc(sketch, "E609", {"start": v(-197.85, -456.36) * mm, "mid": v(-201.97, -457.73) * mm, "end": v(-201.39, -462.03) * mm});
            skArc(sketch, "E610", {"start": v(-189.7, -459.55) * mm, "mid": v(-186.66, -457.86) * mm, "end": v(-185.45, -454.6) * mm});
            skPoint(sketch, "E611.visualSharp", {"position": v(-193.95, -475.13) * mm});
            skArc(sketch, "E611.filletArc", {"start": v(-194.14, -474.79) * mm, "mid": v(-193.9, -475.08) * mm, "end": v(-193.56, -475.25) * mm});
            skPoint(sketch, "E612.visualSharp", {"position": v(-174.83, -395.75) * mm});
            skArc(sketch, "E612.filletArc", {"start": v(-174.83, -395.93) * mm, "mid": v(-174.85, -395.75) * mm, "end": v(-174.9, -395.58) * mm});
            skPoint(sketch, "E613.visualSharp", {"position": v(-185.45, -389.37) * mm});
            skArc(sketch, "E613.filletArc", {"start": v(-185.45, -390.57) * mm, "mid": v(-185.81, -389.8) * mm, "end": v(-186.63, -389.59) * mm});
            skPoint(sketch, "E614.visualSharp", {"position": v(-177.66, -388.31) * mm});
            skArc(sketch, "E614.filletArc", {"start": v(-176.47, -388.1) * mm, "mid": v(-177.16, -388.6) * mm, "end": v(-177.23, -389.45) * mm});
            skPoint(sketch, "E615.visualSharp", {"position": v(-210.95, -393.98) * mm});
            skArc(sketch, "E615.filletArc", {"start": v(-211.14, -393.93) * mm, "mid": v(-210.95, -393.96) * mm, "end": v(-210.75, -393.94) * mm});
            skPoint(sketch, "E616.visualSharp", {"position": v(-220.5, -391.85) * mm});
            skArc(sketch, "E616.filletArc", {"start": v(-219.77, -390.66) * mm, "mid": v(-219.84, -391.57) * mm, "end": v(-219.13, -392.16) * mm});
            skPoint(sketch, "E617.visualSharp", {"position": v(-215.9, -384.4) * mm});
            skArc(sketch, "E617.filletArc", {"start": v(-215.4, -384.34) * mm, "mid": v(-215.83, -384.49) * mm, "end": v(-216.15, -384.8) * mm});
            skPoint(sketch, "E618.visualSharp", {"position": v(-185.96, -380.97) * mm});
            skArc(sketch, "E618.filletArc", {"start": v(-185.9, -380.97) * mm, "mid": v(-185.96, -380.98) * mm, "end": v(-186.02, -380.98) * mm});
            skPoint(sketch, "E619.visualSharp", {"position": v(-172.17, -380.97) * mm});
            skArc(sketch, "E619.filletArc", {"start": v(-173.16, -380.97) * mm, "mid": v(-172.46, -380.69) * mm, "end": v(-172.16, -379.99) * mm});
            skPoint(sketch, "E620.visualSharp", {"position": v(-131.63, -374.5) * mm});
            skArc(sketch, "E620.filletArc", {"start": v(-131.25, -376) * mm, "mid": v(-131.73, -374.87) * mm, "end": v(-132.79, -374.23) * mm});
            skPoint(sketch, "E621.visualSharp", {"position": v(-140.84, -372.38) * mm});
            skArc(sketch, "E621.filletArc", {"start": v(-140.62, -372.43) * mm, "mid": v(-140.84, -372.4) * mm, "end": v(-141.05, -372.42) * mm});
            skPoint(sketch, "E622.visualSharp", {"position": v(-159.6, -376.27) * mm});
            skArc(sketch, "E622.filletArc", {"start": v(-159.6, -375.04) * mm, "mid": v(-159.23, -375.82) * mm, "end": v(-158.4, -376.02) * mm});
            skPoint(sketch, "E623.visualSharp", {"position": v(-159.6, -366.36) * mm});
            skArc(sketch, "E623.filletArc", {"start": v(-159.5, -366.14) * mm, "mid": v(-159.57, -366.36) * mm, "end": v(-159.6, -366.6) * mm});
            skPoint(sketch, "E624.visualSharp", {"position": v(-172.02, -371.35) * mm});
            skArc(sketch, "E624.filletArc", {"start": v(-171.9, -371.14) * mm, "mid": v(-171.99, -371.36) * mm, "end": v(-172.02, -371.6) * mm});
            skPoint(sketch, "E625.visualSharp", {"position": v(-161.73, -352.2) * mm});
            skArc(sketch, "E625.filletArc", {"start": v(-161.9, -352.51) * mm, "mid": v(-161.79, -352.18) * mm, "end": v(-161.8, -351.84) * mm});
            skPoint(sketch, "E626.visualSharp", {"position": v(-150.04, -347.94) * mm});
            skArc(sketch, "E626.filletArc", {"start": v(-150.12, -348.09) * mm, "mid": v(-150.06, -347.94) * mm, "end": v(-150.02, -347.78) * mm});
            skPoint(sketch, "E627.visualSharp", {"position": v(-148.98, -341.22) * mm});
            skArc(sketch, "E627.filletArc", {"start": v(-149.1, -341.93) * mm, "mid": v(-149.2, -341.32) * mm, "end": v(-149.63, -340.89) * mm});
            skPoint(sketch, "E628.visualSharp", {"position": v(-163.5, -333.78) * mm});
            skArc(sketch, "E628.filletArc", {"start": v(-163.06, -334) * mm, "mid": v(-163.5, -333.9) * mm, "end": v(-163.94, -333.99) * mm});
            skPoint(sketch, "E629.visualSharp", {"position": v(-163.14, -345.11) * mm});
            skArc(sketch, "E629.filletArc", {"start": v(-162.92, -346.25) * mm, "mid": v(-163.4, -345.58) * mm, "end": v(-164.24, -345.5) * mm});
            skPoint(sketch, "E630.visualSharp", {"position": v(-183.33, -342.99) * mm});
            skArc(sketch, "E630.filletArc", {"start": v(-183.55, -342.99) * mm, "mid": v(-183.33, -342.96) * mm, "end": v(-183.13, -342.9) * mm});
            skPoint(sketch, "E631.visualSharp", {"position": v(-182.62, -352.2) * mm});
            skArc(sketch, "E631.filletArc", {"start": v(-182.79, -352.2) * mm, "mid": v(-182.62, -352.18) * mm, "end": v(-182.46, -352.14) * mm});
            skLineSegment(sketch, "E632", {"start": v(-174.61, -365.63) * mm, "end": v(-187.8, -370.32) * mm});
            skLineSegment(sketch, "E633", {"start": v(-188.22, -370.38) * mm, "end": v(-196.14, -369.77) * mm});
            skLineSegment(sketch, "E634", {"start": v(-196.14, -369.77) * mm, "end": v(-201.65, -368.14) * mm});
            skLineSegment(sketch, "E635", {"start": v(-198.15, -359.5) * mm, "end": v(-179.67, -359.25) * mm});
            skLineSegment(sketch, "E636", {"start": v(-179.11, -359.42) * mm, "end": v(-174.24, -362.63) * mm});
            skArc(sketch, "E637", {"start": v(-198.15, -359.5) * mm, "mid": v(-202.77, -362.66) * mm, "end": v(-201.65, -368.14) * mm});
            skArc(sketch, "E638", {"start": v(-174.61, -365.63) * mm, "mid": v(-173.49, -364.25) * mm, "end": v(-174.24, -362.63) * mm});
            skPoint(sketch, "E639.visualSharp", {"position": v(-188, -370.4) * mm});
            skArc(sketch, "E639.filletArc", {"start": v(-188.22, -370.38) * mm, "mid": v(-188, -370.37) * mm, "end": v(-187.8, -370.32) * mm});
            skPoint(sketch, "E640.visualSharp", {"position": v(-179.37, -359.25) * mm});
            skArc(sketch, "E640.filletArc", {"start": v(-179.11, -359.42) * mm, "mid": v(-179.38, -359.3) * mm, "end": v(-179.67, -359.25) * mm});
            skLineSegment(sketch, "E641", {"start": v(-222.64, -341.2) * mm, "end": v(-230.84, -333.41) * mm});
            skLineSegment(sketch, "E642", {"start": v(-231.35, -333.16) * mm, "end": v(-238, -331.95) * mm});
            skLineSegment(sketch, "E643", {"start": v(-244.74, -338.26) * mm, "end": v(-240.53, -344.37) * mm});
            skLineSegment(sketch, "E644", {"start": v(-240.53, -344.37) * mm, "end": v(-229.37, -350.68) * mm});
            skArc(sketch, "E645", {"start": v(-238, -331.95) * mm, "mid": v(-242.97, -333.4) * mm, "end": v(-244.74, -338.26) * mm});
            skArc(sketch, "E646", {"start": v(-229.37, -350.68) * mm, "mid": v(-221.73, -348.98) * mm, "end": v(-222.64, -341.2) * mm});
            skPoint(sketch, "E647.visualSharp", {"position": v(-231.06, -333.2) * mm});
            skArc(sketch, "E647.filletArc", {"start": v(-230.84, -333.41) * mm, "mid": v(-231.08, -333.25) * mm, "end": v(-231.35, -333.16) * mm});
            skLineSegment(sketch, "E648", {"start": v(-165.74, -416.99) * mm, "end": v(-167.34, -415.86) * mm});
            skLineSegment(sketch, "E649", {"start": v(-167.68, -414.63) * mm, "end": v(-160.27, -398.26) * mm});
            skLineSegment(sketch, "E650", {"start": v(-165.17, -417.17) * mm, "end": v(-160.73, -417.17) * mm});
            skLineSegment(sketch, "E651", {"start": v(-160.17, -417) * mm, "end": v(-145.09, -406.9) * mm});
            skLineSegment(sketch, "E652", {"start": v(-145.24, -401.24) * mm, "end": v(-148.81, -397.07) * mm});
            skLineSegment(sketch, "E653", {"start": v(-148.81, -397.07) * mm, "end": v(-152.53, -394.7) * mm});
            skArc(sketch, "E654", {"start": v(-145.09, -406.9) * mm, "mid": v(-144.16, -404.04) * mm, "end": v(-145.24, -401.24) * mm});
            skArc(sketch, "E655", {"start": v(-152.53, -394.7) * mm, "mid": v(-157.38, -394.36) * mm, "end": v(-160.27, -398.26) * mm});
            skPoint(sketch, "E656.visualSharp", {"position": v(-165.48, -417.17) * mm});
            skArc(sketch, "E656.filletArc", {"start": v(-165.74, -416.99) * mm, "mid": v(-165.47, -417.12) * mm, "end": v(-165.17, -417.17) * mm});
            skPoint(sketch, "E657.visualSharp", {"position": v(-160.42, -417.17) * mm});
            skArc(sketch, "E657.filletArc", {"start": v(-160.73, -417.17) * mm, "mid": v(-160.44, -417.13) * mm, "end": v(-160.17, -417) * mm});
            skPoint(sketch, "E658.visualSharp", {"position": v(-168.02, -415.38) * mm});
            skArc(sketch, "E658.filletArc", {"start": v(-167.68, -414.63) * mm, "mid": v(-167.73, -415.3) * mm, "end": v(-167.34, -415.86) * mm});
            skLineSegment(sketch, "E659", {"start": v(-196.4, -408.4) * mm, "end": v(-201.2, -404.79) * mm});
            skLineSegment(sketch, "E660", {"start": v(-201.56, -404.62) * mm, "end": v(-206.34, -403.45) * mm});
            skLineSegment(sketch, "E661", {"start": v(-207.27, -403.7) * mm, "end": v(-209.34, -405.66) * mm});
            skLineSegment(sketch, "E662", {"start": v(-209.64, -406.5) * mm, "end": v(-208.99, -412) * mm});
            skLineSegment(sketch, "E663", {"start": v(-208.8, -412.47) * mm, "end": v(-204.9, -417.86) * mm});
            skLineSegment(sketch, "E664", {"start": v(-204.2, -418.27) * mm, "end": v(-200.32, -418.75) * mm});
            skLineSegment(sketch, "E665", {"start": v(-199.54, -418.5) * mm, "end": v(-196.2, -415.54) * mm});
            skLineSegment(sketch, "E666", {"start": v(-195.87, -414.77) * mm, "end": v(-196, -409.17) * mm});
            skPoint(sketch, "E667.visualSharp", {"position": v(-195.86, -415.24) * mm});
            skArc(sketch, "E667.filletArc", {"start": v(-196.2, -415.54) * mm, "mid": v(-195.95, -415.2) * mm, "end": v(-195.87, -414.77) * mm});
            skPoint(sketch, "E668.visualSharp", {"position": v(-196, -408.68) * mm});
            skArc(sketch, "E668.filletArc", {"start": v(-196, -409.17) * mm, "mid": v(-196.1, -408.74) * mm, "end": v(-196.4, -408.4) * mm});
            skPoint(sketch, "E669.visualSharp", {"position": v(-201.36, -404.67) * mm});
            skArc(sketch, "E669.filletArc", {"start": v(-201.2, -404.79) * mm, "mid": v(-201.37, -404.68) * mm, "end": v(-201.56, -404.62) * mm});
            skPoint(sketch, "E670.visualSharp", {"position": v(-206.87, -403.33) * mm});
            skArc(sketch, "E670.filletArc", {"start": v(-206.34, -403.45) * mm, "mid": v(-206.84, -403.46) * mm, "end": v(-207.27, -403.7) * mm});
            skPoint(sketch, "E671.visualSharp", {"position": v(-209.7, -406) * mm});
            skArc(sketch, "E671.filletArc", {"start": v(-209.34, -405.66) * mm, "mid": v(-209.59, -406.05) * mm, "end": v(-209.64, -406.5) * mm});
            skPoint(sketch, "E672.visualSharp", {"position": v(-208.96, -412.26) * mm});
            skArc(sketch, "E672.filletArc", {"start": v(-208.99, -412) * mm, "mid": v(-208.93, -412.25) * mm, "end": v(-208.8, -412.47) * mm});
            skPoint(sketch, "E673.visualSharp", {"position": v(-204.64, -418.21) * mm});
            skArc(sketch, "E673.filletArc", {"start": v(-204.9, -417.86) * mm, "mid": v(-204.6, -418.14) * mm, "end": v(-204.2, -418.27) * mm});
            skPoint(sketch, "E674.visualSharp", {"position": v(-199.88, -418.8) * mm});
            skArc(sketch, "E674.filletArc", {"start": v(-200.32, -418.75) * mm, "mid": v(-199.9, -418.72) * mm, "end": v(-199.54, -418.5) * mm});
            skLineSegment(sketch, "E675", {"start": v(-216.4, -435.48) * mm, "end": v(-223.1, -435.48) * mm});
            skLineSegment(sketch, "E676", {"start": v(-225.04, -444.42) * mm, "end": v(-218.93, -448.58) * mm});
            skLineSegment(sketch, "E677", {"start": v(-212.38, -447.7) * mm, "end": v(-201.66, -441.44) * mm});
            skLineSegment(sketch, "E678", {"start": v(-201.66, -441.44) * mm, "end": v(-194.52, -434.74) * mm});
            skLineSegment(sketch, "E679", {"start": v(-194.52, -434.74) * mm, "end": v(-189.16, -428.63) * mm});
            skLineSegment(sketch, "E680", {"start": v(-193.62, -422.68) * mm, "end": v(-216.4, -435.48) * mm});
            skArc(sketch, "E681", {"start": v(-189.16, -428.63) * mm, "mid": v(-188.78, -423.7) * mm, "end": v(-193.62, -422.68) * mm});
            skArc(sketch, "E682", {"start": v(-218.93, -448.58) * mm, "mid": v(-215.57, -448.79) * mm, "end": v(-212.38, -447.7) * mm});
            skArc(sketch, "E683", {"start": v(-223.1, -435.48) * mm, "mid": v(-227.07, -439.3) * mm, "end": v(-225.04, -444.42) * mm});
            skLineSegment(sketch, "E684", {"start": v(-173.08, -423.5) * mm, "end": v(-151.6, -448.15) * mm});
            skLineSegment(sketch, "E685", {"start": v(-151.33, -448.37) * mm, "end": v(-141.41, -453.84) * mm});
            skLineSegment(sketch, "E686", {"start": v(-141, -453.96) * mm, "end": v(-129.33, -454.68) * mm});
            skLineSegment(sketch, "E687", {"start": v(-129, -454.64) * mm, "end": v(-119.85, -452.07) * mm});
            skLineSegment(sketch, "E688", {"start": v(-119.46, -451.86) * mm, "end": v(-114.7, -447.63) * mm});
            skLineSegment(sketch, "E689", {"start": v(-115.9, -441.29) * mm, "end": v(-122.82, -439.38) * mm});
            skLineSegment(sketch, "E690", {"start": v(-123, -439.35) * mm, "end": v(-134.32, -438.32) * mm});
            skLineSegment(sketch, "E691", {"start": v(-134.42, -438.3) * mm, "end": v(-141.22, -437) * mm});
            skLineSegment(sketch, "E692", {"start": v(-141.5, -436.9) * mm, "end": v(-157.6, -428.49) * mm});
            skLineSegment(sketch, "E693", {"start": v(-157.6, -428.49) * mm, "end": v(-170.7, -419.13) * mm});
            skLineSegment(sketch, "E694", {"start": v(-171.12, -418.26) * mm, "end": v(-171.04, -416.68) * mm});
            skLineSegment(sketch, "E695", {"start": v(-172, -415.63) * mm, "end": v(-173.88, -415.54) * mm});
            skLineSegment(sketch, "E696.trimOffspring", {"start": v(-174.83, -424.16) * mm, "end": v(-174.83, -461.32) * mm});
            skPoint(sketch, "E697.visualSharp", {"position": v(-171, -415.68) * mm});
            skArc(sketch, "E697.filletArc", {"start": v(-171.04, -416.68) * mm, "mid": v(-171.3, -415.96) * mm, "end": v(-172, -415.63) * mm});
            skPoint(sketch, "E698.visualSharp", {"position": v(-171.14, -418.8) * mm});
            skArc(sketch, "E698.filletArc", {"start": v(-171.12, -418.26) * mm, "mid": v(-171.02, -418.75) * mm, "end": v(-170.7, -419.13) * mm});
            skPoint(sketch, "E699.visualSharp", {"position": v(-141.37, -436.97) * mm});
            skArc(sketch, "E699.filletArc", {"start": v(-141.5, -436.9) * mm, "mid": v(-141.36, -436.96) * mm, "end": v(-141.22, -437) * mm});
            skPoint(sketch, "E700.visualSharp", {"position": v(-134.37, -438.31) * mm});
            skArc(sketch, "E700.filletArc", {"start": v(-134.42, -438.3) * mm, "mid": v(-134.37, -438.31) * mm, "end": v(-134.32, -438.32) * mm});
            skPoint(sketch, "E701.visualSharp", {"position": v(-122.9, -439.35) * mm});
            skArc(sketch, "E701.filletArc", {"start": v(-122.82, -439.38) * mm, "mid": v(-122.9, -439.36) * mm, "end": v(-123, -439.35) * mm});
            skPoint(sketch, "E702.visualSharp", {"position": v(-119.63, -452) * mm});
            skArc(sketch, "E702.filletArc", {"start": v(-119.85, -452.07) * mm, "mid": v(-119.64, -451.99) * mm, "end": v(-119.46, -451.86) * mm});
            skPoint(sketch, "E703.visualSharp", {"position": v(-129.16, -454.69) * mm});
            skArc(sketch, "E703.filletArc", {"start": v(-129.33, -454.68) * mm, "mid": v(-129.16, -454.67) * mm, "end": v(-129, -454.64) * mm});
            skPoint(sketch, "E704.visualSharp", {"position": v(-141.22, -453.94) * mm});
            skArc(sketch, "E704.filletArc", {"start": v(-141.41, -453.84) * mm, "mid": v(-141.21, -453.92) * mm, "end": v(-141, -453.96) * mm});
            skPoint(sketch, "E705.visualSharp", {"position": v(-151.49, -448.29) * mm});
            skArc(sketch, "E705.filletArc", {"start": v(-151.6, -448.15) * mm, "mid": v(-151.48, -448.27) * mm, "end": v(-151.33, -448.37) * mm});
            skPoint(sketch, "E706.visualSharp", {"position": v(-174.83, -421.49) * mm});
            skArc(sketch, "E706.filletArc", {"start": v(-173.08, -423.5) * mm, "mid": v(-174.18, -423.22) * mm, "end": v(-174.83, -424.16) * mm});
            skPoint(sketch, "E707.visualSharp", {"position": v(-174.83, -415.5) * mm});
            skArc(sketch, "E707.filletArc", {"start": v(-174.83, -414.55) * mm, "mid": v(-174.55, -415.24) * mm, "end": v(-173.88, -415.54) * mm});
            skLineSegment(sketch, "E708", {"start": v(-274.27, -378.97) * mm, "end": v(-248.74, -376.22) * mm});
            skArc(sketch, "E709", {"start": v(-114.7, -447.63) * mm, "mid": v(-113.33, -444.08) * mm, "end": v(-115.9, -441.29) * mm});
            skLineSegment(sketch, "E710", {"start": v(-248.74, -376.22) * mm, "end": v(-242.07, -373.84) * mm});
            skLineSegment(sketch, "E711", {"start": v(-242.07, -373.84) * mm, "end": v(-234.28, -368.8) * mm});
            skLineSegment(sketch, "E712", {"start": v(-234.28, -368.8) * mm, "end": v(-228.29, -368.8) * mm});
            skLineSegment(sketch, "E713", {"start": v(-224.32, -376.85) * mm, "end": v(-232.6, -388.18) * mm});
            skLineSegment(sketch, "E714", {"start": v(-232.6, -388.18) * mm, "end": v(-232.68, -398.38) * mm});
            skLineSegment(sketch, "E715", {"start": v(-231.65, -399.4) * mm, "end": v(-226.49, -399.24) * mm});
            skLineSegment(sketch, "E716", {"start": v(-277.48, -383.6) * mm, "end": v(-277.36, -387.73) * mm});
            skLineSegment(sketch, "E717", {"start": v(-266.47, -391.6) * mm, "end": v(-250.07, -384.1) * mm});
            skLineSegment(sketch, "E718", {"start": v(-250.07, -384.1) * mm, "end": v(-241.3, -382.47) * mm});
            skLineSegment(sketch, "E719", {"start": v(-241.3, -382.47) * mm, "end": v(-241.3, -393.76) * mm});
            skLineSegment(sketch, "E720", {"start": v(-241.53, -394.39) * mm, "end": v(-245.04, -398.67) * mm});
            skLineSegment(sketch, "E721", {"start": v(-245.73, -399.03) * mm, "end": v(-249.1, -399.34) * mm});
            skLineSegment(sketch, "E722", {"start": v(-249.82, -400.91) * mm, "end": v(-248.28, -403.09) * mm});
            skLineSegment(sketch, "E723", {"start": v(-248.37, -404.35) * mm, "end": v(-279.7, -437.68) * mm});
            skLineSegment(sketch, "E724", {"start": v(-274.93, -440.1) * mm, "end": v(-267.27, -435.96) * mm});
            skLineSegment(sketch, "E725", {"start": v(-267.04, -435.78) * mm, "end": v(-255.64, -424.17) * mm});
            skLineSegment(sketch, "E726", {"start": v(-255.5, -424) * mm, "end": v(-244.24, -406.41) * mm});
            skLineSegment(sketch, "E727", {"start": v(-242.4, -407.03) * mm, "end": v(-245.87, -450.64) * mm});
            skLineSegment(sketch, "E728", {"start": v(-245.87, -450.64) * mm, "end": v(-248.16, -457.53) * mm});
            skLineSegment(sketch, "E729", {"start": v(-248.16, -457.53) * mm, "end": v(-248.58, -463.74) * mm});
            skLineSegment(sketch, "E730", {"start": v(-243.63, -468.27) * mm, "end": v(-241.74, -468.27) * mm});
            skLineSegment(sketch, "E731", {"start": v(-236.79, -461.11) * mm, "end": v(-236.16, -429.49) * mm});
            skLineSegment(sketch, "E732", {"start": v(-236.15, -429.36) * mm, "end": v(-232.88, -406.65) * mm});
            skLineSegment(sketch, "E733", {"start": v(-231.95, -405.8) * mm, "end": v(-231.46, -405.77) * mm});
            skLineSegment(sketch, "E734", {"start": v(-230.66, -406.1) * mm, "end": v(-226.77, -410.37) * mm});
            skPoint(sketch, "E735", {"position": v(-220.03, -403.42) * mm});
            skArc(sketch, "E736", {"start": v(-220.03, -403.42) * mm, "mid": v(-222.61, -400.33) * mm, "end": v(-226.49, -399.24) * mm});
            skArc(sketch, "E737", {"start": v(-226.77, -410.37) * mm, "mid": v(-220.67, -409.54) * mm, "end": v(-220.03, -403.42) * mm});
            skArc(sketch, "E738", {"start": v(-224.32, -376.85) * mm, "mid": v(-223.52, -371.45) * mm, "end": v(-228.29, -368.8) * mm});
            skArc(sketch, "E739", {"start": v(-277.36, -387.73) * mm, "mid": v(-272.7, -391.88) * mm, "end": v(-266.47, -391.6) * mm});
            skArc(sketch, "E740", {"start": v(-274.27, -378.97) * mm, "mid": v(-276.94, -380.55) * mm, "end": v(-277.48, -383.6) * mm});
            skArc(sketch, "E741", {"start": v(-279.8, -438.94) * mm, "mid": v(-277.59, -440.45) * mm, "end": v(-274.93, -440.1) * mm});
            skPoint(sketch, "E742.visualSharp", {"position": v(-280.2, -438.2) * mm});
            skArc(sketch, "E742.filletArc", {"start": v(-279.7, -437.68) * mm, "mid": v(-279.97, -438.3) * mm, "end": v(-279.8, -438.94) * mm});
            skPoint(sketch, "E743.visualSharp", {"position": v(-267.14, -435.89) * mm});
            skArc(sketch, "E743.filletArc", {"start": v(-267.27, -435.96) * mm, "mid": v(-267.15, -435.88) * mm, "end": v(-267.04, -435.78) * mm});
            skPoint(sketch, "E744.visualSharp", {"position": v(-255.56, -424.1) * mm});
            skArc(sketch, "E744.filletArc", {"start": v(-255.64, -424.17) * mm, "mid": v(-255.57, -424.1) * mm, "end": v(-255.5, -424) * mm});
            skPoint(sketch, "E745.visualSharp", {"position": v(-242.09, -403.04) * mm});
            skArc(sketch, "E745.filletArc", {"start": v(-242.4, -407.03) * mm, "mid": v(-243.08, -406) * mm, "end": v(-244.24, -406.41) * mm});
            skPoint(sketch, "E746.visualSharp", {"position": v(-247.81, -403.75) * mm});
            skArc(sketch, "E746.filletArc", {"start": v(-248.37, -404.35) * mm, "mid": v(-248.1, -403.73) * mm, "end": v(-248.28, -403.09) * mm});
            skPoint(sketch, "E747.visualSharp", {"position": v(-250.82, -399.5) * mm});
            skArc(sketch, "E747.filletArc", {"start": v(-249.1, -399.34) * mm, "mid": v(-249.9, -399.92) * mm, "end": v(-249.82, -400.91) * mm});
            skPoint(sketch, "E748.visualSharp", {"position": v(-245.3, -399) * mm});
            skArc(sketch, "E748.filletArc", {"start": v(-245.73, -399.03) * mm, "mid": v(-245.35, -398.92) * mm, "end": v(-245.04, -398.67) * mm});
            skPoint(sketch, "E749.visualSharp", {"position": v(-241.3, -394.11) * mm});
            skArc(sketch, "E749.filletArc", {"start": v(-241.53, -394.39) * mm, "mid": v(-241.36, -394.1) * mm, "end": v(-241.3, -393.76) * mm});
            skPoint(sketch, "E750.visualSharp", {"position": v(-232.69, -399.42) * mm});
            skArc(sketch, "E750.filletArc", {"start": v(-232.68, -398.38) * mm, "mid": v(-232.38, -399.1) * mm, "end": v(-231.65, -399.4) * mm});
            skPoint(sketch, "E751.visualSharp", {"position": v(-230.98, -405.74) * mm});
            skArc(sketch, "E751.filletArc", {"start": v(-230.66, -406.1) * mm, "mid": v(-231.02, -405.84) * mm, "end": v(-231.46, -405.77) * mm});
            skPoint(sketch, "E752.visualSharp", {"position": v(-236.16, -429.42) * mm});
            skArc(sketch, "E752.filletArc", {"start": v(-236.15, -429.36) * mm, "mid": v(-236.15, -429.42) * mm, "end": v(-236.16, -429.49) * mm});
            skArc(sketch, "E753", {"start": v(-241.74, -468.27) * mm, "mid": v(-238.18, -465.43) * mm, "end": v(-236.79, -461.11) * mm});
            skArc(sketch, "E754", {"start": v(-248.58, -463.74) * mm, "mid": v(-246.98, -466.97) * mm, "end": v(-243.63, -468.27) * mm});
            skPoint(sketch, "E755.visualSharp", {"position": v(-232.77, -405.84) * mm});
            skArc(sketch, "E755.filletArc", {"start": v(-231.95, -405.8) * mm, "mid": v(-232.57, -406.06) * mm, "end": v(-232.88, -406.65) * mm});
            skText(sketch, "E756", { "text": "LUCK", "fontName": "OpenSans-Regular.ttf"});
            skText(sketch, "E757", { "text": "LONGEVITY", "fontName": "OpenSans-Regular.ttf"});
            skText(sketch, "E758", { "text": "HAPPINESS", "fontName": "OpenSans-Regular.ttf"});
            skText(sketch, "E759", { "text": "PROSPERITY", "fontName": "OpenSans-Regular.ttf"});
            skArc(sketch, "E760", {"start": v(-239.63, -237.07) * mm, "mid": v(-236.44, -238.1) * mm, "end": v(-233.66, -236.25) * mm});
            skLineSegment(sketch, "E761.trimOffspring", {"start": v(-172.2, -111.8) * mm, "end": v(-173.04, -112.28) * mm});
            skLineSegment(sketch, "E762.trimOffspring", {"start": v(-171.3, -125.78) * mm, "end": v(-168.35, -124.46) * mm});
            skPoint(sketch, "E763.visualSharp", {"position": v(-172.7, -126.42) * mm});
            skPoint(sketch, "E764.visualSharp", {"position": v(-174.64, -127.28) * mm});
            skLineSegment(sketch, "E765", {"start": v(-147.44, -158.8) * mm, "end": v(-147.44, -163.6) * mm});
            skLineSegment(sketch, "E766", {"start": v(-146.4, -158.53) * mm, "end": v(-146.4, -163.62) * mm});
            skLineSegment(sketch, "E767.trimOffspring", {"start": v(-148.53, -157.81) * mm, "end": v(-152.61, -158.19) * mm});
            skLineSegment(sketch, "E768.trimOffspring", {"start": v(-145.4, -164.62) * mm, "end": v(-143.22, -164.63) * mm});
            skPoint(sketch, "E769.visualSharp", {"position": v(-146.4, -157.62) * mm});
            skArc(sketch, "E769.filletArc", {"start": v(-145.5, -157.53) * mm, "mid": v(-146.14, -157.85) * mm, "end": v(-146.4, -158.53) * mm});
            skPoint(sketch, "E770.visualSharp", {"position": v(-146.4, -164.62) * mm});
            skArc(sketch, "E770.filletArc", {"start": v(-146.4, -163.62) * mm, "mid": v(-146.1, -164.33) * mm, "end": v(-145.4, -164.62) * mm});
            skPoint(sketch, "E771.visualSharp", {"position": v(-147.44, -157.71) * mm});
            skArc(sketch, "E771.filletArc", {"start": v(-147.44, -158.8) * mm, "mid": v(-147.77, -158.07) * mm, "end": v(-148.53, -157.81) * mm});
            skPoint(sketch, "E772.visualSharp", {"position": v(-147.44, -164.61) * mm});
            skArc(sketch, "E772.filletArc", {"start": v(-148.44, -164.6) * mm, "mid": v(-147.73, -164.31) * mm, "end": v(-147.44, -163.6) * mm});
            skLineSegment(sketch, "E773", {"start": v(-189.02, -170.98) * mm, "end": v(-189.02, -175.4) * mm});
            skLineSegment(sketch, "E774", {"start": v(-188.27, -169.98) * mm, "end": v(-188.27, -174.36) * mm});
            skLineSegment(sketch, "E775.trimOffspring", {"start": v(-189.66, -176.34) * mm, "end": v(-198.37, -179.66) * mm});
            skLineSegment(sketch, "E776.trimOffspring", {"start": v(-190.36, -170.04) * mm, "end": v(-199.13, -173.23) * mm});
            skPoint(sketch, "E777.visualSharp", {"position": v(-188.27, -169.28) * mm});
            skArc(sketch, "E777.filletArc", {"start": v(-187.6, -169.04) * mm, "mid": v(-188.08, -169.4) * mm, "end": v(-188.27, -169.98) * mm});
            skPoint(sketch, "E778.visualSharp", {"position": v(-189.02, -169.55) * mm});
            skArc(sketch, "E778.filletArc", {"start": v(-189.02, -170.98) * mm, "mid": v(-189.44, -170.16) * mm, "end": v(-190.36, -170.04) * mm});
            skPoint(sketch, "E779.visualSharp", {"position": v(-188.27, -175.8) * mm});
            skArc(sketch, "E779.filletArc", {"start": v(-188.27, -174.36) * mm, "mid": v(-187.83, -175.18) * mm, "end": v(-186.9, -175.3) * mm});
            skPoint(sketch, "E780.visualSharp", {"position": v(-189.02, -176.1) * mm});
            skArc(sketch, "E780.filletArc", {"start": v(-189.66, -176.34) * mm, "mid": v(-189.2, -175.97) * mm, "end": v(-189.02, -175.4) * mm});
            skLineSegment(sketch, "E781", {"start": v(-175.14, -105.85) * mm, "end": v(-175.14, -112.86) * mm});
            skLineSegment(sketch, "E782", {"start": v(-174.53, -111.4) * mm, "end": v(-174.53, -104.76) * mm});
            skLineSegment(sketch, "E783.trimOffspring", {"start": v(-176.53, -104.93) * mm, "end": v(-187.3, -109.41) * mm});
            skLineSegment(sketch, "E784.trimOffspring", {"start": v(-175.66, -113.74) * mm, "end": v(-186.5, -119.78) * mm});
            skPoint(sketch, "E785.visualSharp", {"position": v(-175.14, -104.35) * mm});
            skArc(sketch, "E785.filletArc", {"start": v(-175.14, -105.85) * mm, "mid": v(-175.59, -105.02) * mm, "end": v(-176.53, -104.93) * mm});
            skPoint(sketch, "E786.visualSharp", {"position": v(-174.53, -104.1) * mm});
            skArc(sketch, "E786.filletArc", {"start": v(-173.92, -103.84) * mm, "mid": v(-174.36, -104.2) * mm, "end": v(-174.53, -104.76) * mm});
            skPoint(sketch, "E787.visualSharp", {"position": v(-174.53, -113.11) * mm});
            skArc(sketch, "E787.filletArc", {"start": v(-174.53, -111.4) * mm, "mid": v(-174.04, -112.27) * mm, "end": v(-173.04, -112.28) * mm});
            skPoint(sketch, "E788.visualSharp", {"position": v(-175.14, -113.45) * mm});
            skArc(sketch, "E788.filletArc", {"start": v(-175.66, -113.74) * mm, "mid": v(-175.28, -113.37) * mm, "end": v(-175.14, -112.86) * mm});
            skLineSegment(sketch, "E789", {"start": v(199.74, -370.75) * mm, "end": v(199.74, -374.5) * mm});
            skLineSegment(sketch, "E790", {"start": v(200.52, -370.45) * mm, "end": v(200.52, -374.02) * mm});
            skLineSegment(sketch, "E791.trimOffspring", {"start": v(201.42, -369.45) * mm, "end": v(220.66, -367.34) * mm});
            skLineSegment(sketch, "E792.trimOffspring", {"start": v(201.7, -375) * mm, "end": v(213.74, -372.93) * mm});
            skPoint(sketch, "E793.visualSharp", {"position": v(200.52, -369.55) * mm});
            skArc(sketch, "E793.filletArc", {"start": v(201.42, -369.45) * mm, "mid": v(200.78, -369.78) * mm, "end": v(200.52, -370.45) * mm});
            skPoint(sketch, "E794.visualSharp", {"position": v(199.74, -375.35) * mm});
            skArc(sketch, "E794.filletArc", {"start": v(198.9, -375.5) * mm, "mid": v(199.5, -375.15) * mm, "end": v(199.74, -374.5) * mm});
            skPoint(sketch, "E795.visualSharp", {"position": v(200.52, -375.21) * mm});
            skArc(sketch, "E795.filletArc", {"start": v(200.52, -374.02) * mm, "mid": v(200.88, -374.79) * mm, "end": v(201.7, -375) * mm});
            skPoint(sketch, "E796.visualSharp", {"position": v(199.74, -369.64) * mm});
            skArc(sketch, "E796.filletArc", {"start": v(199.74, -370.75) * mm, "mid": v(199.4, -370) * mm, "end": v(198.63, -369.76) * mm});
            skLineSegment(sketch, "E797", {"start": v(197.89, -438.94) * mm, "end": v(197.89, -442) * mm});
            skLineSegment(sketch, "E798", {"start": v(198.9, -438.79) * mm, "end": v(198.9, -441.73) * mm});
            skLineSegment(sketch, "E799.trimOffspring", {"start": v(196.84, -437.94) * mm, "end": v(166.54, -439.45) * mm});
            skLineSegment(sketch, "E800.trimOffspring", {"start": v(196.98, -443) * mm, "end": v(186.83, -443.91) * mm});
            skPoint(sketch, "E801.visualSharp", {"position": v(198.9, -437.83) * mm});
            skArc(sketch, "E801.filletArc", {"start": v(199.84, -437.79) * mm, "mid": v(199.17, -438.1) * mm, "end": v(198.9, -438.79) * mm});
            skPoint(sketch, "E802.visualSharp", {"position": v(198.9, -442.83) * mm});
            skArc(sketch, "E802.filletArc", {"start": v(198.9, -441.73) * mm, "mid": v(199.22, -442.47) * mm, "end": v(199.98, -442.73) * mm});
            skPoint(sketch, "E803.visualSharp", {"position": v(197.89, -442.92) * mm});
            skArc(sketch, "E803.filletArc", {"start": v(196.98, -443) * mm, "mid": v(197.62, -442.68) * mm, "end": v(197.89, -442) * mm});
            skPoint(sketch, "E804.visualSharp", {"position": v(197.89, -437.88) * mm});
            skArc(sketch, "E804.filletArc", {"start": v(197.89, -438.94) * mm, "mid": v(197.58, -438.21) * mm, "end": v(196.84, -437.94) * mm});
            skArc(sketch, "E805.trimOffspring", {"start": v(200.05, -147.79) * mm, "mid": v(203.7, -139.63) * mm, "end": v(207.01, -131.35) * mm});
            skPoint(sketch, "E806.visualSharp", {"position": v(236.53, -239.17) * mm});
            skArc(sketch, "E806.filletArc", {"start": v(235.76, -237.98) * mm, "mid": v(236.56, -238.44) * mm, "end": v(237.4, -238.05) * mm});
            skArc(sketch, "E807", {"start": v(252.22, -82.93) * mm, "mid": v(256.41, -80.2) * mm, "end": v(256.8, -75.2) * mm});
            skArc(sketch, "E808", {"start": v(240.46, -104.07) * mm, "mid": v(243.58, -100.33) * mm, "end": v(240.6, -96.47) * mm});
            skLineSegment(sketch, "E809", {"start": v(150.97, -205.38) * mm, "end": v(152.3, -214.99) * mm});
            skLineSegment(sketch, "E810", {"start": v(215.23, -173.01) * mm, "end": v(236.4, -178.81) * mm});
            skLineSegment(sketch, "E811", {"start": v(243.94, -405.05) * mm, "end": v(250, -402.83) * mm});
            skPoint(sketch, "E812.visualSharp", {"position": v(252.07, -402.07) * mm});
            skArc(sketch, "E812.filletArc", {"start": v(250, -402.83) * mm, "mid": v(250.66, -401.96) * mm, "end": v(250.14, -401.01) * mm});
            skPoint(sketch, "E813.visualSharp", {"position": v(235.67, -393.08) * mm});
            const initialGuessF0  = {"E756": [-0.24438, -0.28207, 1, 0, 0.025], "E757": [0.12517, -0.27707, 1, 0, 0.02], "E758": [0.10837, -0.52087, 1, 0, 0.025], "E759": [-0.30036, -0.52087, 1, 0, 0.025]};
            skSetInitialGuess(sketch, initialGuessF0);
            skSolve(sketch);
        }
        {
            var Q0;
            Q0=makeQuery(id+"F0.imprint","IMPRINT",FACE,{"disambiguationData":[TD([[makeQuery(id+"F0.imprint","IMPRINT",EDGE,{"derivedFrom":sQuery(id+"F0.wireOp",EDGE,"E1.bottom")}),-1.0]])]});
            var Q1;
            Q1=makeQuery(id+"F0.imprint","IMPRINT",FACE,{"disambiguationData":[TD([[makeQuery(id+"F0.imprint","IMPRINT",EDGE,{"derivedFrom":sQuery(id+"F0.wireOp",EDGE,"E0.bottom")}),-1.0]])]});
            extrude(context, id + "F1", {"entities" : qUnion([Q0, Q1]), "depth" : 3 * mm, "offsetDistance" : 25 * mm});
        }
    });
